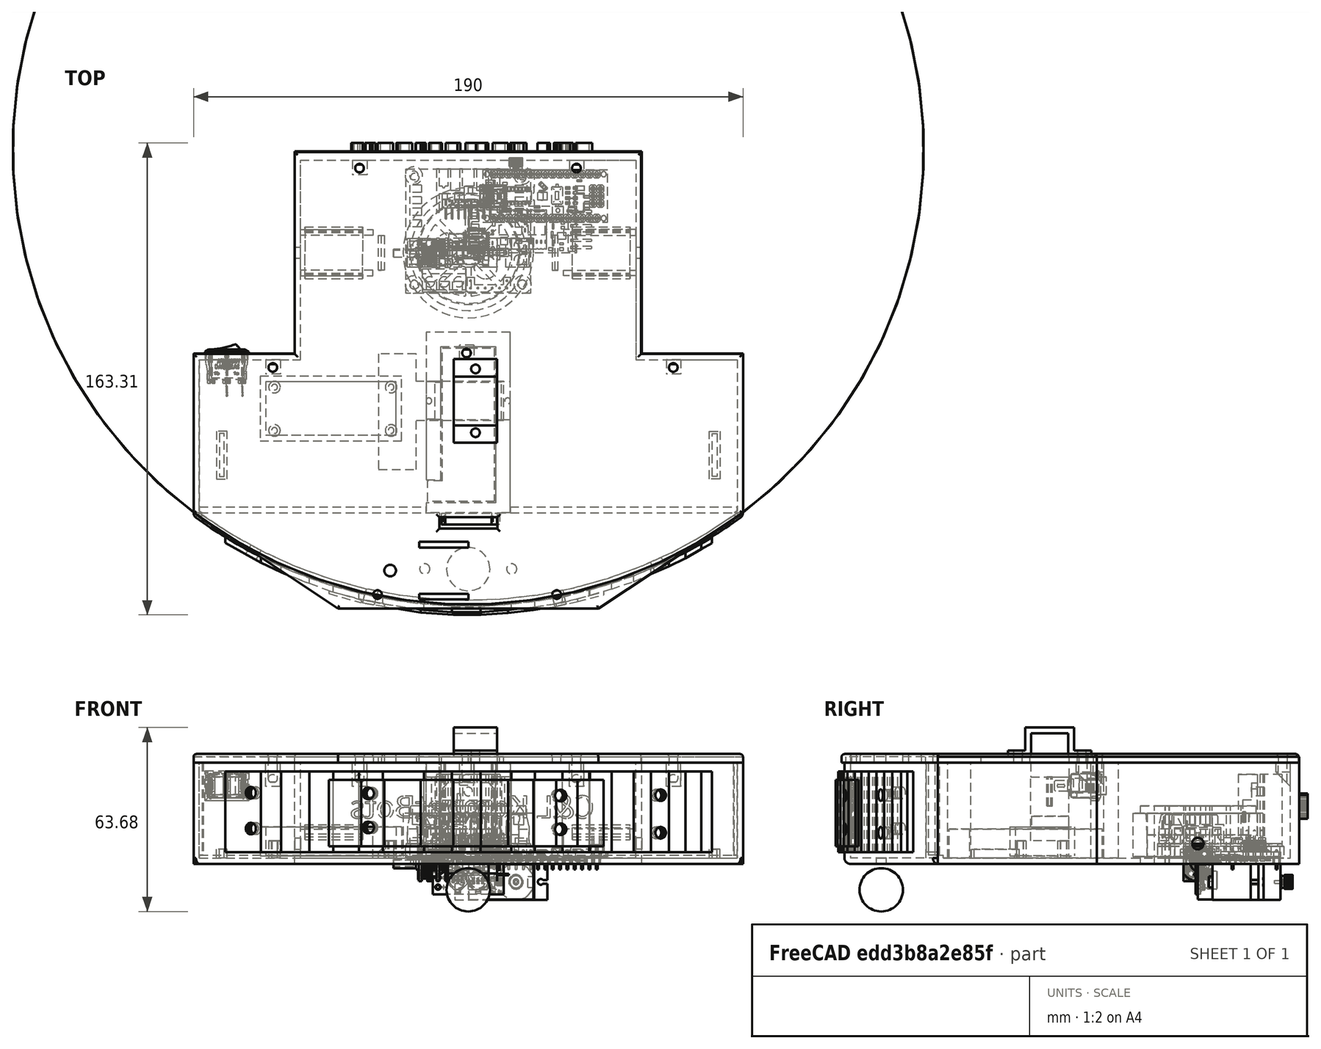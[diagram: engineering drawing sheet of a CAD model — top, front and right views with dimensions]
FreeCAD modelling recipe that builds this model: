
FCSTD DOCUMENT  (FreeCAD 0.20R29410 (Git))
Label: zero_bot
License: All rights reserved
LicenseURL: http://en.wikipedia.org/wiki/All_rights_reserved
objects: Part::Feature×118, Part::Extrusion×50, Sketcher::SketchObject×43, Part::Cut×26, Part::MultiFuse×22, App::Part×10, Part::Box×3, Part::Chamfer×2, Mesh::Feature×2, Part::Part2DObjectPython×1, Part::Fuse×1, Part::Fillet×1, Part::Thickness×1, Part::Sphere×1
note: 269 computed .brp shape members not serialized (recipe doc carries the construction recipe); baked Part::Feature solids carry a one-line shape summary decoded from their .brp

FEATURE [Part::Feature] Part__Feature101  label="Lid Screw Hole001"
  Placement = pos=(159.5,0,0) rot=(0,0,1;0rad)
  shape: bbox 5 x 5 x 8.25 mm, 13 faces (baked)
FEATURE [Part::Feature] Part__Feature102  label="Lid Screw Hole002"
  Placement = pos=(51,69,0) rot=(0,0,1;0rad)
  shape: bbox 5 x 5 x 8.25 mm, 13 faces (baked)
FEATURE [Part::Feature] Part__Feature103  label="Lid Screw Hole003"
  Placement = pos=(126,69,0) rot=(0,0,1;0rad)
  shape: bbox 5 x 5 x 8.25 mm, 13 faces (baked)
FEATURE [Part::Feature] Part__Feature104  label="Lid Screw Hole004"
  Placement = pos=(-120,-158,0) rot=(0,0,1;3.14159rad)
  shape: bbox 5 x 5 x 8.25 mm, 13 faces (baked)
FEATURE [Part::Feature] Part__Feature105  label="Lid Screw Hole005"
  Placement = pos=(-58,-158,0) rot=(0,0,1;3.14159rad)
  shape: bbox 5 x 5 x 8.25 mm, 13 faces (baked)
FEATURE [Part::Feature] Part__Feature106  label="Lid Screw Hole006"
  Placement = pos=(88,5,0) rot=(0,0,1;0rad)
  shape: bbox 5 x 5 x 8.25 mm, 13 faces (baked)
FEATURE [Part::Part2DObjectPython] ShapeString  # Draft 2D object (typed FeaturePython)
  FontFile = <path>
  MakeFace = true
  Placement = pos=(43.52,35,15.82) rot=(0,0.707107,0.707107;3.14159rad)
  Size = 5
  String = C&L KombatBots
  Tracking = 0
FEATURE [Part::Extrusion] Extrude026  label="RobotText"
  Base = -> ShapeString
  Dir = (1e-16,1,4e-16)
  DirMode = 2
  FaceMakerClass = Part::FaceMakerBullseye
  LengthFwd = 3
  LengthRev = 0
  Solid = false
  Symmetric = false
FEATURE [Sketcher::SketchObject] Sketch001
  FullyConstrained = true
  sketch-geometry (10):
    g0: LineSegment StartX=-60 StartY=35 StartZ=0 EndX=60 EndY=35 EndZ=0
    g1: LineSegment StartX=60 StartY=35 StartZ=0 EndX=60 EndY=-35 EndZ=0
    g2: LineSegment StartX=60 StartY=-35 StartZ=0 EndX=95 EndY=-35 EndZ=0
    g3: LineSegment StartX=95 StartY=-35 StartZ=0 EndX=95 EndY=-90 EndZ=0
    g4: LineSegment StartX=95 StartY=-90 StartZ=0 EndX=45 EndY=-123.166 EndZ=0
    g5: LineSegment StartX=45 StartY=-123.166 StartZ=0 EndX=-45 EndY=-123.166 EndZ=0
    g6: LineSegment StartX=-45 StartY=-123.166 StartZ=0 EndX=-95 EndY=-90 EndZ=0
    g7: LineSegment StartX=-95 StartY=-90 StartZ=0 EndX=-95 EndY=-35 EndZ=0
    g8: LineSegment StartX=-95 StartY=-35 StartZ=0 EndX=-60 EndY=-35 EndZ=0
    g9: LineSegment StartX=-60 StartY=-35 StartZ=0 EndX=-60 EndY=35 EndZ=0
  constraints (29):
    c: Horizontal(g0)
    c: Coincident(g0,g1)
    c: Vertical(g1)
    c: Coincident(g1,g2)
    c: Coincident(g2,g3)
    c: Coincident(g3,g4)
    c: Coincident(g4,g5)
    c: Coincident(g5,g6)
    c: Coincident(g6,g7)
    c: Coincident(g7,g8)
    c: Horizontal(g8)
    c: Coincident(g8,g9)
    c: Coincident(g9,g0)
    c: DistanceX(g0,g0) = 120
    c: Vertical(g9)
    c: DistanceY(g9,g9) = 70
    c: DistanceX(g8,g8) = 35
    c: Vertical(g7)
    c: DistanceX(g5,g5) = 90
    c: Horizontal(g5)
    c: Vertical(g3)
    c: DistanceY(g3,g3) = 55
    c: Horizontal(g2)
    c: Equal(g2,g8)
    c: Equal(g9,g1)
    c: Distance(g4) = 60
    c: Equal(g4,g6)
    c: Equal(g3,g7)
    c: Symmetric(g1,g0,g-1)
FEATURE [Part::Extrusion] Extrude001  label="Floor"
  Base = -> Sketch001
  Dir = (0,0,1)
  DirMode = 2
  FaceMakerClass = Part::FaceMakerBullseye
  LengthFwd = 2
  LengthRev = 0
  Solid = true
  Symmetric = false
FEATURE [Sketcher::SketchObject] Sketch002
  FullyConstrained = true
  sketch-geometry (22):
    g0: LineSegment StartX=-60 StartY=35 StartZ=0 EndX=60 EndY=35 EndZ=0
    g1: LineSegment StartX=60 StartY=35 StartZ=0 EndX=60 EndY=-35 EndZ=0
    g2: LineSegment StartX=60 StartY=-35 StartZ=0 EndX=95 EndY=-35 EndZ=0
    g3: LineSegment StartX=95 StartY=-35 StartZ=0 EndX=95 EndY=-90 EndZ=0
    g4: LineSegment StartX=95 StartY=-90 StartZ=0 EndX=45 EndY=-123.166 EndZ=0
    g5: LineSegment StartX=45 StartY=-123.166 StartZ=0 EndX=-45 EndY=-123.166 EndZ=0
    g6: LineSegment StartX=-45 StartY=-123.166 StartZ=0 EndX=-95 EndY=-90 EndZ=0
    g7: LineSegment StartX=-95 StartY=-90 StartZ=0 EndX=-95 EndY=-35 EndZ=0
    g8: LineSegment StartX=-95 StartY=-35 StartZ=0 EndX=-60 EndY=-35 EndZ=0
    g9: LineSegment StartX=-60 StartY=-35 StartZ=0 EndX=-60 EndY=35 EndZ=0
    g10: LineSegment StartX=-58 StartY=32 StartZ=0 EndX=58 EndY=32 EndZ=0
    g11: LineSegment StartX=58 StartY=32 StartZ=0 EndX=58 EndY=-37 EndZ=0
    g12: LineSegment StartX=58 StartY=-37 StartZ=0 EndX=93 EndY=-37 EndZ=0
    g13: LineSegment StartX=93 StartY=-37 StartZ=0 EndX=93 EndY=-89.3266 EndZ=0
    g14: LineSegment StartX=93 StartY=-89.3266 StartZ=0 EndX=45 EndY=-121.166 EndZ=0
    g15: LineSegment StartX=45 StartY=-121.166 StartZ=0 EndX=-45 EndY=-121.166 EndZ=0
    g16: LineSegment StartX=-45 StartY=-121.166 StartZ=0 EndX=-93 EndY=-89.3266 EndZ=0
    g17: LineSegment StartX=-93 StartY=-89.3266 StartZ=0 EndX=-93 EndY=-37 EndZ=0
    g18: LineSegment StartX=-93 StartY=-37 StartZ=0 EndX=-58 EndY=-37 EndZ=0
    g19: LineSegment StartX=-58 StartY=-37 StartZ=0 EndX=-58 EndY=32 EndZ=0
    g20: LineSegment StartX=-45 StartY=-121.166 StartZ=0 EndX=-45 EndY=-123.166 EndZ=0
    g21: LineSegment StartX=45 StartY=-121.166 StartZ=0 EndX=45 EndY=-123.166 EndZ=0
  constraints (63):
    c: Horizontal(g0)
    c: Coincident(g0,g1)
    c: Vertical(g1)
    c: Coincident(g1,g2)
    c: Horizontal(g2)
    c: Coincident(g2,g3)
    c: Vertical(g3)
    c: Coincident(g3,g4)
    c: Coincident(g4,g5)
    c: Horizontal(g5)
    c: Coincident(g5,g6)
    c: Coincident(g6,g7)
    c: Vertical(g7)
    c: Coincident(g7,g8)
    c: Horizontal(g8)
    c: Coincident(g8,g9)
    c: Coincident(g9,g0)
    c: Vertical(g9)
    c: Symmetric(g0,g1,g-1)
    c: DistanceX(g0,g0) = 120
    c: DistanceY(g1,g1) = 70
    c: Equal(g9,g1)
    c: DistanceX(g2,g2) = 35
    c: Equal(g2,g8)
    c: DistanceY(g3,g3) = 55
    c: DistanceX(g5,g5) = 90
    c: Distance(g4) = 60
    c: Equal(g4,g6)
    c: Equal(g3,g7)
    c: Horizontal(g10)
    c: Coincident(g11,g10)
    c: Vertical(g11)
    c: Coincident(g11,g12)
    c: Horizontal(g12)
    c: Coincident(g12,g13)
    c: Vertical(g13)
    c: Coincident(g13,g14)
    c: Coincident(g14,g15)
    c: Horizontal(g15)
    c: Coincident(g15,g16)
    c: Coincident(g16,g17)
    c: Vertical(g17)
    c: Coincident(g17,g18)
    c: Horizontal(g18)
    c: Coincident(g18,g19)
    c: Coincident(g19,g10)
    c: Vertical(g19)
    c: Distance(g10,g0) = 3
    c: Distance(g10,g9) = 2
    c: Distance(g17,g8) = 2
    c: Distance(g16,g7) = 2
    c: Distance(g15,g5) = 2
    c: Distance(g13,g3) = 2
    c: Distance(g12,g2) = 2
    c: Distance(g10,g1) = 2
    c: Coincident(g20,g15)
    c: Coincident(g20,g5)
    c: Coincident(g21,g14)
    c: Coincident(g21,g4)
    c: Vertical(g21)
    c: Vertical(g20)
    c: Parallel(g16,g6)
    c: Parallel(g14,g4)
FEATURE [Part::Extrusion] Extrude002  label="Walls"
  Base = -> Sketch002
  Dir = (0,0,1)
  DirMode = 2
  FaceMakerClass = Part::FaceMakerBullseye
  LengthFwd = 35
  LengthRev = 0
  Solid = true
  Symmetric = false
FEATURE [Part::MultiFuse] Fusion004  label="Body"
  Refine = true
  Shapes = -> [Extrude002,Extrude001]
FEATURE [Sketcher::SketchObject] Sketch003
  FullyConstrained = false
  MapMode = 5
  Placement = pos=(0,0,2) rot=(0,0,1;0rad)
  Support = -> [Fusion004]
  sketch-geometry (36):
    g0: GeomPoint X=25 Y=0 Z=0
    g1: LineSegment StartX=33 StartY=6 StartZ=0 EndX=58 EndY=6 EndZ=0
    g2: LineSegment StartX=58 StartY=6 StartZ=0 EndX=58 EndY=8 EndZ=0
    g3: LineSegment StartX=58 StartY=8 StartZ=0 EndX=33 EndY=8 EndZ=0
    g4: LineSegment StartX=33 StartY=8 StartZ=0 EndX=33 EndY=6 EndZ=0
    g5: GeomPoint X=-25 Y=0 Z=0
    g6: LineSegment StartX=33 StartY=6 StartZ=0 EndX=25 EndY=0 EndZ=0
    g7: GeomPoint X=25 Y=0 Z=0
    g8: LineSegment StartX=32.5993 StartY=-6.5 StartZ=0 EndX=25 EndY=0 EndZ=0
    g9: GeomPoint X=-25 Y=0 Z=0
    g10: GeomPoint X=-25 Y=0 Z=0
    g11: GeomPoint X=25 Y=0 Z=0
    g12: LineSegment StartX=33 StartY=-6 StartZ=0 EndX=58 EndY=-6 EndZ=0
    g13: LineSegment StartX=58 StartY=-6 StartZ=0 EndX=58 EndY=-8 EndZ=0
    g14: LineSegment StartX=58 StartY=-8 StartZ=0 EndX=33 EndY=-8 EndZ=0
    g15: LineSegment StartX=33 StartY=-8 StartZ=0 EndX=33 EndY=-6 EndZ=0
    g16: LineSegment StartX=33 StartY=-6 StartZ=0 EndX=25 EndY=0 EndZ=0
    g17: GeomPoint X=25 Y=0 Z=0
    g18: LineSegment StartX=32.5993 StartY=6.5 StartZ=0 EndX=25 EndY=0 EndZ=0
    g19: GeomPoint X=-25 Y=0 Z=0
    g20: LineSegment StartX=-33 StartY=6 StartZ=0 EndX=-58 EndY=6 EndZ=0
    g21: LineSegment StartX=-58 StartY=6 StartZ=0 EndX=-58 EndY=8 EndZ=0
    g22: LineSegment StartX=-58 StartY=8 StartZ=0 EndX=-33 EndY=8 EndZ=0
    g23: LineSegment StartX=-33 StartY=8 StartZ=0 EndX=-33 EndY=6 EndZ=0
    g24: LineSegment StartX=-33 StartY=6 StartZ=0 EndX=-25 EndY=0 EndZ=0
    g25: GeomPoint X=-25 Y=0 Z=0
    g26: LineSegment StartX=-32.5993 StartY=-6.5 StartZ=0 EndX=-25 EndY=0 EndZ=0
    g27: GeomPoint X=-25 Y=0 Z=0
    g28: LineSegment StartX=-33 StartY=-6 StartZ=0 EndX=-58 EndY=-6 EndZ=0
    g29: LineSegment StartX=-58 StartY=-6 StartZ=0 EndX=-58 EndY=-8 EndZ=0
    g30: LineSegment StartX=-58 StartY=-8 StartZ=0 EndX=-33 EndY=-8 EndZ=0
    g31: LineSegment StartX=-33 StartY=-8 StartZ=0 EndX=-33 EndY=-6 EndZ=0
    g32: LineSegment StartX=-33 StartY=-6 StartZ=0 EndX=-25 EndY=0 EndZ=0
    g33: GeomPoint X=-25 Y=0 Z=0
    g34: LineSegment StartX=-32.5993 StartY=6.5 StartZ=0 EndX=-25 EndY=0 EndZ=0
    g35: LineSegment StartX=-33 StartY=8 StartZ=0 EndX=-33 EndY=-8 EndZ=0
  constraints (60):
    c: PointOnObject(g0,g-1)
    c: Distance(g-1,g0) = 25
    c: Coincident(g1,g2)
    c: Coincident(g2,g3)
    c: Coincident(g3,g4)
    c: Coincident(g4,g1)
    c: Horizontal(g1)
    c: Horizontal(g3)
    c: Vertical(g2)
    c: Vertical(g4)
    c: DistanceY(g4,g4) = 2
    c: DistanceX(g1,g1) = 25
    c: Coincident(g6,g1)
    c: Coincident(g6,g0)
    c: Distance(g6) = 10
    c: DistanceY(g-1,g1) = 6
    c: Coincident(g8,g7)
    c: Distance(g8) = 10
    c: Coincident(g12,g13)
    c: Coincident(g13,g14)
    c: Coincident(g14,g15)
    c: Coincident(g15,g12)
    c: Horizontal(g12)
    c: Horizontal(g14)
    c: Vertical(g13)
    c: Vertical(g15)
    c: Coincident(g16,g12)
    c: Coincident(g16,g11)
    c: Distance(g16) = 10
    c: Coincident(g18,g17)
    c: Distance(g18) = 10
    c: Coincident(g20,g21)
    c: Coincident(g21,g22)
    c: Coincident(g22,g23)
    c: Coincident(g23,g20)
    c: Horizontal(g20)
    c: Horizontal(g22)
    c: Vertical(g21)
    c: Vertical(g23)
    c: Coincident(g24,g20)
    c: Coincident(g24,g19)
    c: Distance(g24) = 10
    c: Coincident(g26,g25)
    c: Distance(g26) = 10
    c: Coincident(g28,g29)
    c: Coincident(g29,g30)
    c: Coincident(g30,g31)
    c: Coincident(g31,g28)
    c: Horizontal(g28)
    c: Horizontal(g30)
    c: Vertical(g29)
    c: Vertical(g31)
    c: Coincident(g32,g28)
    c: Coincident(g32,g27)
    c: Distance(g32) = 10
    c: Coincident(g34,g33)
    c: Distance(g34) = 10
    c: Coincident(g35,g22)
    c: Coincident(g35,g30)
    c: Vertical(g35)
FEATURE [Part::Extrusion] Extrude003  label="motorWalls"
  Base = -> Sketch003
  Dir = (0,0,1)
  DirMode = 2
  FaceMakerClass = Part::FaceMakerBullseye
  LengthFwd = 10
  LengthRev = 0
  Solid = true
  Symmetric = false
FEATURE [Sketcher::SketchObject] Sketch004
  FullyConstrained = false
  MapMode = 5
  Placement = pos=(0,0,2) rot=(0,0,1;0rad)
  Support = -> [Fusion004]
  sketch-geometry (10):
    g0: LineSegment StartX=-31 StartY=6 StartZ=0 EndX=-29 EndY=6 EndZ=0
    g1: LineSegment StartX=-29 StartY=6 StartZ=0 EndX=-29 EndY=-6 EndZ=0
    g2: LineSegment StartX=-29 StartY=-6 StartZ=0 EndX=-31 EndY=-6 EndZ=0
    g3: LineSegment StartX=-31 StartY=-6 StartZ=0 EndX=-31 EndY=6 EndZ=0
    g4: GeomPoint X=-30 Y=0 Z=0
    g5: LineSegment StartX=31 StartY=6 StartZ=0 EndX=29 EndY=6 EndZ=0
    g6: LineSegment StartX=29 StartY=6 StartZ=0 EndX=29 EndY=-6 EndZ=0
    g7: LineSegment StartX=29 StartY=-6 StartZ=0 EndX=31 EndY=-6 EndZ=0
    g8: LineSegment StartX=31 StartY=-6 StartZ=0 EndX=31 EndY=6 EndZ=0
    g9: GeomPoint X=30 Y=0 Z=0
  constraints (22):
    c: Coincident(g0,g1)
    c: Coincident(g1,g2)
    c: Coincident(g2,g3)
    c: Coincident(g3,g0)
    c: Horizontal(g0)
    c: Horizontal(g2)
    c: Vertical(g1)
    c: Vertical(g3)
    c: PointOnObject(g4,g-1)
    c: Distance(g-1,g4) = 30
    c: Symmetric(g0,g2,g4)
    c: DistanceX(g0,g0) = 2
    c: DistanceY(g1,g1) = 12
    c: Coincident(g5,g6)
    c: Coincident(g6,g7)
    c: Coincident(g7,g8)
    c: Coincident(g8,g5)
    c: Horizontal(g5)
    c: Horizontal(g7)
    c: Vertical(g6)
    c: Vertical(g8)
    c: Symmetric(g5,g7,g9)
FEATURE [Part::Extrusion] Extrude004
  Base = -> Sketch004
  Dir = (0,0,1)
  DirMode = 2
  FaceMakerClass = Part::FaceMakerBullseye
  LengthFwd = 3
  LengthRev = 0
  Solid = true
  Symmetric = false
FEATURE [Part::Chamfer] Chamfer  label="MotorSlotter"
  Base = -> Extrude004
  Edges = 2 edges r=1: [Edge12,Edge24]
FEATURE [Part::MultiFuse] Fusion001  label="MotorHolders"
  Refine = true
  Shapes = -> [Chamfer,Extrude003]
FEATURE [Part::MultiFuse] Fusion005
  Refine = true
  Shapes = -> [Fusion001,Fusion004]
FEATURE [Sketcher::SketchObject] Sketch005
  FullyConstrained = true
  MapMode = 5
  Placement = pos=(0,0,2) rot=(0,0,1;0rad)
  Support = -> [Fusion005]
  sketch-geometry (8):
    g0: Circle CenterX=-18.8 CenterY=26.75 CenterZ=0 NormalX=0 NormalY=0 NormalZ=1 AngleXU=0 Radius=3
    g1: Circle CenterX=-18.8 CenterY=26.75 CenterZ=0 NormalX=0 NormalY=0 NormalZ=1 AngleXU=0 Radius=1.5
    g2: Circle CenterX=18.8 CenterY=26.75 CenterZ=0 NormalX=0 NormalY=0 NormalZ=1 AngleXU=0 Radius=3
    g3: Circle CenterX=18.8 CenterY=26.75 CenterZ=0 NormalX=0 NormalY=0 NormalZ=1 AngleXU=0 Radius=1.5
    g4: Circle CenterX=18.8 CenterY=-11 CenterZ=0 NormalX=0 NormalY=0 NormalZ=1 AngleXU=0 Radius=3
    g5: Circle CenterX=18.8 CenterY=-11 CenterZ=0 NormalX=0 NormalY=0 NormalZ=1 AngleXU=0 Radius=1.5
    g6: Circle CenterX=-18.8 CenterY=-11 CenterZ=0 NormalX=0 NormalY=0 NormalZ=1 AngleXU=0 Radius=3
    g7: Circle CenterX=-18.8 CenterY=-11 CenterZ=0 NormalX=0 NormalY=0 NormalZ=1 AngleXU=0 Radius=1.5
  constraints (20):
    c: Coincident(g1,g0)
    c: Coincident(g3,g2)
    c: Coincident(g5,g4)
    c: Coincident(g7,g6)
    c: DistanceX(g-2,g6) = -18.8
    c: Diameter(g7) = 3
    c: Diameter(g6) = 6
    c: DistanceY(g-1,g6) = -11
    c: DistanceY(g-1,g4) = -11
    c: DistanceX(g-2,g4) = 18.8
    c: Diameter(g5) = 3
    c: Diameter(g4) = 6
    c: DistanceY(g-1,g2) = 26.75
    c: DistanceY(g-1,g0) = 26.75
    c: DistanceX(g-2,g2) = 18.8
    c: DistanceX(g-2,g0) = -18.8
    c: Diameter(g1) = 3
    c: Diameter(g0) = 6
    c: Diameter(g2) = 6
    c: Diameter(g3) = 3
FEATURE [Part::Extrusion] Extrude005  label="L289N Holder"
  Base = -> Sketch005
  Dir = (0,0,1)
  DirMode = 2
  FaceMakerClass = Part::FaceMakerBullseye
  LengthFwd = 4
  LengthRev = 0
  Solid = true
  Symmetric = false
FEATURE [Part::MultiFuse] Fusion006
  Refine = true
  Shapes = -> [Extrude005,Fusion005]
FEATURE [Sketcher::SketchObject] Sketch006
  FullyConstrained = true
  MapMode = 5
  Placement = pos=(60,0,0) rot=(0.57735,0.57735,0.57735;2.0944rad)
  Support = -> [Fusion006]
  sketch-geometry (1):
    g0: Circle CenterX=0 CenterY=7 CenterZ=0 NormalX=0 NormalY=0 NormalZ=1 AngleXU=0 Radius=2
  constraints (3):
    c: PointOnObject(g0,g-2)
    c: Diameter(g0) = 4
    c: Distance(g0,g-1) = 7
FEATURE [Part::Extrusion] Extrude006
  Base = -> Sketch006
  Dir = (1,0,0)
  DirMode = 2
  FaceMakerClass = Part::FaceMakerBullseye
  LengthFwd = 10
  LengthRev = 0
  Solid = true
  Symmetric = true
FEATURE [Sketcher::SketchObject] Sketch007
  FullyConstrained = true
  MapMode = 5
  Placement = pos=(-60,0,0) rot=(0.57735,-0.57735,-0.57735;2.0944rad)
  Support = -> [Fusion006]
  sketch-geometry (1):
    g0: Circle CenterX=0 CenterY=7 CenterZ=0 NormalX=0 NormalY=0 NormalZ=1 AngleXU=0 Radius=2
  constraints (3):
    c: PointOnObject(g0,g-2)
    c: Diameter(g0) = 4
    c: Distance(g-1,g0) = 7
FEATURE [Part::Extrusion] Extrude007
  Base = -> Sketch007
  Dir = (-1,0,0)
  DirMode = 2
  FaceMakerClass = Part::FaceMakerBullseye
  LengthFwd = 10
  LengthRev = 0
  Solid = true
  Symmetric = true
FEATURE [Part::MultiFuse] Fusion007  label="Motor Gaps"
  Refine = true
  Shapes = -> [Extrude006,Extrude007]
FEATURE [Part::Cut] Cut005
  Base = -> Fusion006
  Refine = true
  Tool = -> Fusion007
FEATURE [Sketcher::SketchObject] Sketch008
  FullyConstrained = false
  MapMode = 5
  Placement = pos=(0,-35,0) rot=(0,0.707107,0.707107;3.14159rad)
  Support = -> [Cut005]
  sketch-geometry (4):
    g0: LineSegment StartX=90.8327 StartY=31.6367 StartZ=0 EndX=76.0827 EndY=31.6367 EndZ=0
    g1: LineSegment StartX=76.0827 StartY=31.6367 StartZ=0 EndX=76.0827 EndY=21.8867 EndZ=0
    g2: LineSegment StartX=76.0827 StartY=21.8867 StartZ=0 EndX=90.8327 EndY=21.8867 EndZ=0
    g3: LineSegment StartX=90.8327 StartY=21.8867 StartZ=0 EndX=90.8327 EndY=31.6367 EndZ=0
  constraints (8):
    c: Coincident(g0,g1)
    c: Coincident(g1,g2)
    c: Coincident(g2,g3)
    c: Coincident(g3,g0)
    c: Horizontal(g0)
    c: Horizontal(g2)
    c: Vertical(g1)
    c: Vertical(g3)
FEATURE [Part::Extrusion] Extrude008  label="InterruptGap"
  Base = -> Sketch008
  Dir = (0,1,-2e-16)
  DirMode = 2
  FaceMakerClass = Part::FaceMakerBullseye
  LengthFwd = 10
  LengthRev = 0
  Solid = true
  Symmetric = true
FEATURE [Part::Cut] Cut006
  Base = -> Cut005
  Refine = true
  Tool = -> Extrude008
FEATURE [Sketcher::SketchObject] Sketch009
  FullyConstrained = false
  MapMode = 5
  Placement = pos=(0,0,2) rot=(0,0,1;0rad)
  Support = -> [Cut006]
  sketch-geometry (20):
    g0: LineSegment StartX=83.4 StartY=-61.75 StartZ=0 EndX=87 EndY=-61.75 EndZ=0
    g1: LineSegment StartX=87 StartY=-61.75 StartZ=0 EndX=87 EndY=-78.25 EndZ=0
    g2: LineSegment StartX=87 StartY=-78.25 StartZ=0 EndX=83.4 EndY=-78.25 EndZ=0
    g3: LineSegment StartX=83.4 StartY=-78.25 StartZ=0 EndX=83.4 EndY=-61.75 EndZ=0
    g4: LineSegment StartX=84.4 StartY=-62.6 StartZ=0 EndX=86 EndY=-62.6 EndZ=0
    g5: LineSegment StartX=86 StartY=-62.6 StartZ=0 EndX=86 EndY=-77.4 EndZ=0
    g6: LineSegment StartX=86 StartY=-77.4 StartZ=0 EndX=84.4 EndY=-77.4 EndZ=0
    g7: LineSegment StartX=84.4 StartY=-77.4 StartZ=0 EndX=84.4 EndY=-62.6 EndZ=0
    g8: GeomPoint X=93 Y=-70 Z=0
    g9: LineSegment StartX=-0.686599 StartY=-70 StartZ=0 EndX=93 EndY=-70 EndZ=0
    g10: LineSegment StartX=-83.4 StartY=-61.75 StartZ=0 EndX=-87 EndY=-61.75 EndZ=0
    g11: LineSegment StartX=-87 StartY=-61.75 StartZ=0 EndX=-87 EndY=-78.25 EndZ=0
    g12: LineSegment StartX=-87 StartY=-78.25 StartZ=0 EndX=-83.4 EndY=-78.25 EndZ=0
    g13: LineSegment StartX=-83.4 StartY=-78.25 StartZ=0 EndX=-83.4 EndY=-61.75 EndZ=0
    g14: LineSegment StartX=-84.4 StartY=-62.6 StartZ=0 EndX=-86 EndY=-62.6 EndZ=0
    g15: LineSegment StartX=-86 StartY=-62.6 StartZ=0 EndX=-86 EndY=-77.4 EndZ=0
    g16: LineSegment StartX=-86 StartY=-77.4 StartZ=0 EndX=-84.4 EndY=-77.4 EndZ=0
    g17: LineSegment StartX=-84.4 StartY=-77.4 StartZ=0 EndX=-84.4 EndY=-62.6 EndZ=0
    g18: GeomPoint X=-93 Y=-70 Z=0
    g19: LineSegment StartX=0.686599 StartY=-70 StartZ=0 EndX=-93 EndY=-70 EndZ=0
  constraints (46):
    c: Coincident(g0,g1)
    c: Coincident(g1,g2)
    c: Coincident(g2,g3)
    c: Coincident(g3,g0)
    c: Horizontal(g0)
    c: Horizontal(g2)
    c: Vertical(g1)
    c: Vertical(g3)
    c: Coincident(g4,g5)
    c: Coincident(g5,g6)
    c: Coincident(g6,g7)
    c: Coincident(g7,g4)
    c: Horizontal(g4)
    c: Horizontal(g6)
    c: Vertical(g7)
    c: DistanceX(g-2,g8) = 93
    c: DistanceY(g-1,g8) = -70
    c: Distance(g8,g1) = 6
    c: Coincident(g9,g8)
    c: Symmetric(g1,g0,g9)
    c: DistanceY(g1,g1) = 16.5
    c: Symmetric(g4,g5,g9)
    c: DistanceY(g5,g5) = 14.8
    c: DistanceX(g0,g0) = 3.6
    c: DistanceX(g4,g4) = 1.6
    c: Distance(g4,g1) = 1
    c: Coincident(g10,g11)
    c: Coincident(g11,g12)
    c: Coincident(g12,g13)
    c: Coincident(g13,g10)
    c: Horizontal(g10)
    c: Horizontal(g12)
    c: Vertical(g11)
    c: Vertical(g13)
    c: Coincident(g14,g15)
    c: Coincident(g15,g16)
    c: Coincident(g16,g17)
    c: Coincident(g17,g14)
    c: Horizontal(g14)
    c: Horizontal(g16)
    c: Vertical(g17)
    c: Distance(g18,g11) = 6
    c: Coincident(g19,g18)
    c: Symmetric(g11,g10,g19)
    c: Symmetric(g14,g15,g19)
    c: Distance(g14,g11) = 1
FEATURE [Part::Extrusion] Extrude009  label="HitSensorHolders"
  Base = -> Sketch009
  Dir = (0,0,1)
  DirMode = 2
  FaceMakerClass = Part::FaceMakerBullseye
  LengthFwd = 3
  LengthRev = 0
  Solid = true
  Symmetric = false
FEATURE [Part::MultiFuse] Fusion008
  Refine = true
  Shapes = -> [Cut006,Extrude009]
FEATURE [Sketcher::SketchObject] Sketch010
  FullyConstrained = true
  sketch-geometry (11):
    g0: LineSegment StartX=-14.5 StartY=-78.5 StartZ=0 EndX=-9.5 EndY=-78.5 EndZ=0
    g1: LineSegment StartX=-9.5 StartY=-78.5 StartZ=0 EndX=-9.5 EndY=-32.5 EndZ=0
    g2: LineSegment StartX=-9.5 StartY=-32.5 StartZ=0 EndX=9.5 EndY=-32.5 EndZ=0
    g3: LineSegment StartX=9.5 StartY=-32.5 StartZ=0 EndX=9.5 EndY=-86.5 EndZ=0
    g4: LineSegment StartX=9.5 StartY=-86.5 StartZ=0 EndX=-14.5 EndY=-86.5 EndZ=0
    g5: LineSegment StartX=-14.5 StartY=-86.5 StartZ=0 EndX=-14.5 EndY=-91.5 EndZ=0
    g6: LineSegment StartX=-14.5 StartY=-91.5 StartZ=0 EndX=14.5 EndY=-91.5 EndZ=0
    g7: LineSegment StartX=14.5 StartY=-91.5 StartZ=0 EndX=14.5 EndY=-27.5 EndZ=0
    g8: LineSegment StartX=14.5 StartY=-27.5 StartZ=0 EndX=-14.5 EndY=-27.5 EndZ=0
    g9: LineSegment StartX=-14.5 StartY=-27.5 StartZ=0 EndX=-14.5 EndY=-78.5 EndZ=0
    g10: GeomPoint X=0 Y=-59.5 Z=0
  constraints (30):
    c: Horizontal(g0)
    c: Coincident(g0,g1)
    c: Vertical(g1)
    c: Coincident(g1,g2)
    c: Horizontal(g2)
    c: Coincident(g2,g3)
    c: Vertical(g3)
    c: Coincident(g3,g4)
    c: Horizontal(g4)
    c: Coincident(g4,g5)
    c: Vertical(g5)
    c: Coincident(g5,g6)
    c: Horizontal(g6)
    c: Coincident(g6,g7)
    c: Vertical(g7)
    c: Coincident(g7,g8)
    c: Horizontal(g8)
    c: Coincident(g8,g9)
    c: Coincident(g9,g0)
    c: Vertical(g9)
    c: DistanceX(g2,g2) = 19
    c: PointOnObject(g10,g-2)
    c: DistanceY(g10,g-1) = 59.5
    c: Symmetric(g3,g1,g10)
    c: Symmetric(g6,g8,g10)
    c: DistanceX(g8,g8) = 29
    c: DistanceY(g3,g3) = 54
    c: DistanceY(g7,g7) = 64
    c: DistanceY(g1,g1) = 46
    c: DistanceX(g6,g6) = 29
FEATURE [Part::Extrusion] Extrude010  label="Battery Gap"
  Base = -> Sketch010
  Dir = (0,0,1)
  DirMode = 2
  FaceMakerClass = Part::FaceMakerBullseye
  LengthFwd = 35
  LengthRev = 0
  Solid = true
  Symmetric = false
FEATURE [Part::MultiFuse] Fusion009
  Refine = true
  Shapes = -> [Extrude010,Fusion008]
FEATURE [Sketcher::SketchObject] Sketch011
  FullyConstrained = false
  MapMode = 5
  Placement = pos=(0,0,2) rot=(0,0,1;0rad)
  Support = -> [Fusion009]
  sketch-geometry (13):
    g0: LineSegment StartX=-52.8 StartY=-54 StartZ=0 EndX=0 EndY=-54 EndZ=0
    g1: LineSegment StartX=-52.8 StartY=-54 StartZ=0 EndX=-84.748 EndY=-54 EndZ=0
    g2: Circle CenterX=-66.9946 CenterY=-46.5 CenterZ=0 NormalX=0 NormalY=0 NormalZ=1 AngleXU=0 Radius=1
    g3: Circle CenterX=-66.9946 CenterY=-46.5 CenterZ=0 NormalX=0 NormalY=0 NormalZ=1 AngleXU=0 Radius=2
    g4: Circle CenterX=-66.9946 CenterY=-61.5 CenterZ=0 NormalX=0 NormalY=0 NormalZ=1 AngleXU=0 Radius=1
    g5: Circle CenterX=-66.9946 CenterY=-61.5 CenterZ=0 NormalX=0 NormalY=0 NormalZ=1 AngleXU=0 Radius=2
    g6: GeomPoint X=-25.3 Y=-54 Z=0
    g7: Circle CenterX=-26.6711 CenterY=-46.5 CenterZ=0 NormalX=0 NormalY=0 NormalZ=1 AngleXU=0 Radius=1
    g8: Circle CenterX=-26.6711 CenterY=-46.5 CenterZ=0 NormalX=0 NormalY=0 NormalZ=1 AngleXU=0 Radius=2
    g9: Circle CenterX=-26.6711 CenterY=-61.5 CenterZ=0 NormalX=0 NormalY=0 NormalZ=1 AngleXU=0 Radius=1
    g10: Circle CenterX=-26.6711 CenterY=-61.5 CenterZ=0 NormalX=0 NormalY=0 NormalZ=1 AngleXU=0 Radius=2
    g11: LineSegment StartX=-52.8 StartY=-54 StartZ=0 EndX=0 EndY=-54 EndZ=0
    g12: GeomPoint X=-25.3 Y=-54 Z=0
  constraints (24):
    c: DistanceY(g0,g-1) = 54
    c: PointOnObject(g0,g-2)
    c: Horizontal(g0)
    c: Coincident(g1,g0)
    c: Horizontal(g1)
    c: Coincident(g3,g2)
    c: Diameter(g2) = 2
    c: Diameter(g3) = 4
    c: Distance(g2,g1) = 7.5
    c: Coincident(g5,g4)
    c: Diameter(g4) = 2
    c: Diameter(g5) = 4
    c: PointOnObject(g6,g0)
    c: DistanceX(g6,g-1) = 25.3
    c: Coincident(g8,g7)
    c: Diameter(g7) = 2
    c: Diameter(g8) = 4
    c: Distance(g7,g0) = 7.5
    c: Horizontal(g11)
    c: PointOnObject(g12,g11)
    c: Coincident(g10,g9)
    c: Diameter(g9) = 2
    c: Diameter(g10) = 4
    c: Distance(g9,g11) = 7.5
FEATURE [Part::Extrusion] Extrude011  label="Arduino Holder"
  Base = -> Sketch011
  Dir = (0,0,1)
  DirMode = 2
  FaceMakerClass = Part::FaceMakerBullseye
  LengthFwd = 6
  LengthRev = 0
  Solid = true
  Symmetric = false
FEATURE [Part::MultiFuse] Fusion010
  Refine = true
  Shapes = -> [Fusion009,Extrude011]
FEATURE [Sketcher::SketchObject] Sketch012
  FullyConstrained = true
  MapMode = 5
  Placement = pos=(0,-91.5,0) rot=(1,0,0;1.5708rad)
  Support = -> [Extrude010]
  sketch-geometry (10):
    g0: LineSegment StartX=8 StartY=35 StartZ=0 EndX=10 EndY=35 EndZ=0
    g1: LineSegment StartX=10 StartY=35 StartZ=0 EndX=10 EndY=2 EndZ=0
    g2: LineSegment StartX=10 StartY=2 StartZ=0 EndX=-10 EndY=2 EndZ=0
    g3: LineSegment StartX=-10 StartY=2 StartZ=0 EndX=-10 EndY=35 EndZ=0
    g4: LineSegment StartX=-10 StartY=35 StartZ=0 EndX=-8 EndY=35 EndZ=0
    g5: LineSegment StartX=-8 StartY=35 StartZ=0 EndX=-8 EndY=4 EndZ=0
    g6: LineSegment StartX=-8 StartY=4 StartZ=0 EndX=8 EndY=4 EndZ=0
    g7: LineSegment StartX=8 StartY=4 StartZ=0 EndX=8 EndY=35 EndZ=0
    g8: GeomPoint X=0 Y=2 Z=0
    g9: LineSegment StartX=0 StartY=2 StartZ=0 EndX=0 EndY=0 EndZ=0
  constraints (28):
    c: Horizontal(g0)
    c: Coincident(g0,g1)
    c: Vertical(g1)
    c: Coincident(g1,g2)
    c: Coincident(g2,g3)
    c: Vertical(g3)
    c: Coincident(g3,g4)
    c: Horizontal(g4)
    c: Coincident(g4,g5)
    c: Vertical(g5)
    c: Coincident(g5,g6)
    c: Horizontal(g6)
    c: Coincident(g6,g7)
    c: Coincident(g7,g0)
    c: Vertical(g7)
    c: DistanceX(g0,g0) = 2
    c: Equal(g4,g0)
    c: DistanceX(g6,g6) = 16
    c: DistanceY(g1,g1) = 33
    c: Equal(g3,g1)
    c: Distance(g6,g2) = 2
    c: Horizontal(g2)
    c: PointOnObject(g8,g2)
    c: DistanceX(g8,g1) = 10
    c: DistanceY(g-1,g1) = 2
    c: Coincident(g9,g8)
    c: Coincident(g9,g-1)
    c: Vertical(g9)
FEATURE [Part::Extrusion] Extrude012  label="Bluetooth Module Holder"
  Base = -> Sketch012
  Dir = (0,-1,2e-16)
  DirMode = 2
  FaceMakerClass = Part::FaceMakerBullseye
  LengthFwd = 4
  LengthRev = 0
  Solid = true
  Symmetric = false
FEATURE [Part::MultiFuse] Fusion011
  Refine = true
  Shapes = -> [Fusion010,Extrude012]
FEATURE [Sketcher::SketchObject] Sketch013
  FullyConstrained = false
  MapMode = 5
  Placement = pos=(4.907e-13,3.136e-13,35) rot=(0,0,1;0rad)
  Support = -> [Fusion011]
  sketch-geometry (8):
    g0: LineSegment StartX=8 StartY=-92.5 StartZ=0 EndX=8.5 EndY=-92.5 EndZ=0
    g1: LineSegment StartX=8.5 StartY=-92.5 StartZ=0 EndX=8.5 EndY=-94.7 EndZ=0
    g2: LineSegment StartX=8.5 StartY=-94.7 StartZ=0 EndX=8 EndY=-94.7 EndZ=0
    g3: LineSegment StartX=8 StartY=-94.7 StartZ=0 EndX=8 EndY=-92.5 EndZ=0
    g4: LineSegment StartX=-8 StartY=-92.5 StartZ=0 EndX=-8.5 EndY=-92.5 EndZ=0
    g5: LineSegment StartX=-8.5 StartY=-92.5 StartZ=0 EndX=-8.5 EndY=-94.7 EndZ=0
    g6: LineSegment StartX=-8.5 StartY=-94.7 StartZ=0 EndX=-8 EndY=-94.7 EndZ=0
    g7: LineSegment StartX=-8 StartY=-94.7 StartZ=0 EndX=-8 EndY=-92.5 EndZ=0
  constraints (20):
    c: Coincident(g0,g1)
    c: Coincident(g1,g2)
    c: Coincident(g2,g3)
    c: Coincident(g3,g0)
    c: Horizontal(g0)
    c: Horizontal(g2)
    c: Vertical(g1)
    c: Vertical(g3)
    c: DistanceY(g1,g1) = 2.2
    c: DistanceX(g0,g0) = 0.5
    c: DistanceX(g-2,g0) = 8
    c: DistanceY(g-1,g0) = -92.5
    c: Coincident(g4,g5)
    c: Coincident(g5,g6)
    c: Coincident(g6,g7)
    c: Coincident(g7,g4)
    c: Horizontal(g4)
    c: Horizontal(g6)
    c: Vertical(g5)
    c: Vertical(g7)
FEATURE [Part::Extrusion] Extrude013  label="Bluetooth Module Slotter"
  Base = -> Sketch013
  Dir = (1.4e-14,9e-15,1)
  DirMode = 2
  FaceMakerClass = Part::FaceMakerBullseye
  LengthFwd = -32
  LengthRev = 0
  Solid = true
  Symmetric = false
FEATURE [Part::Cut] Cut007
  Base = -> Fusion011
  Refine = true
  Tool = -> Extrude013
FEATURE [Sketcher::SketchObject] Sketch014
  FullyConstrained = false
  MapMode = 5
  Placement = pos=(0,-37,0) rot=(1,0,0;1.5708rad)
  Support = -> [Cut007]
  sketch-geometry (4):
    g0: LineSegment StartX=-91.0267 StartY=31.7549 StartZ=0 EndX=-86.0267 EndY=31.7549 EndZ=0
    g1: LineSegment StartX=-86.0267 StartY=31.7549 StartZ=0 EndX=-86.0267 EndY=26.7549 EndZ=0
    g2: LineSegment StartX=-86.0267 StartY=26.7549 StartZ=0 EndX=-91.0267 EndY=26.7549 EndZ=0
    g3: LineSegment StartX=-91.0267 StartY=26.7549 StartZ=0 EndX=-91.0267 EndY=31.7549 EndZ=0
  constraints (10):
    c: Coincident(g0,g1)
    c: Coincident(g1,g2)
    c: Coincident(g2,g3)
    c: Coincident(g3,g0)
    c: Horizontal(g0)
    c: Horizontal(g2)
    c: Vertical(g1)
    c: Vertical(g3)
    c: DistanceX(g0,g0) = 5
    c: DistanceY(g1,g1) = 5
FEATURE [Part::Extrusion] Extrude014
  Base = -> Sketch014
  Dir = (0,-1,2e-16)
  DirMode = 2
  FaceMakerClass = Part::FaceMakerBullseye
  LengthFwd = 5
  LengthRev = 0
  Solid = true
  Symmetric = false
FEATURE [Part::Chamfer] Chamfer001  label="Bot Screw Holder"
  Base = -> Extrude014
  Edges = 1 edges r=4.99: [Edge10]
FEATURE [Sketcher::SketchObject] Sketch015
  FullyConstrained = true
  MapMode = 5
  Placement = pos=(0,7e-15,31.7549) rot=(0,0,1;0rad)
  Support = -> [Chamfer001]
  sketch-geometry (1):
    g0: Circle CenterX=-88.6 CenterY=-39.7 CenterZ=0 NormalX=0 NormalY=0 NormalZ=1 AngleXU=0 Radius=1.5
  constraints (3):
    c: Diameter(g0) = 3
    c: DistanceX(g-2,g0) = -88.6
    c: DistanceY(g-1,g0) = -39.7
FEATURE [Part::Extrusion] Extrude015  label="Screw Hole"
  Base = -> Sketch015
  Dir = (0,2e-16,1)
  DirMode = 2
  FaceMakerClass = Part::FaceMakerBullseye
  LengthFwd = -8
  LengthRev = 0
  Placement = pos=(0,0,4.5) rot=(0,0,1;0rad)
  Solid = true
  Symmetric = false
FEATURE [Sketcher::SketchObject] Sketch016
  FullyConstrained = false
  MapMode = 5
  Placement = pos=(0,7e-15,31.7549) rot=(0,0,1;0rad)
  Support = -> [Chamfer001]
  sketch-geometry (4):
    g0: LineSegment StartX=-91.0267 StartY=-37 StartZ=0 EndX=-86.0267 EndY=-37 EndZ=0
    g1: LineSegment StartX=-86.0267 StartY=-37 StartZ=0 EndX=-86.0267 EndY=-42 EndZ=0
    g2: LineSegment StartX=-86.0267 StartY=-42 StartZ=0 EndX=-91.0267 EndY=-42 EndZ=0
    g3: LineSegment StartX=-91.0267 StartY=-42 StartZ=0 EndX=-91.0267 EndY=-37 EndZ=0
  constraints (10):
    c: Coincident(g0,g1)
    c: Coincident(g1,g2)
    c: Coincident(g2,g3)
    c: Coincident(g3,g0)
    c: Horizontal(g0)
    c: Horizontal(g2)
    c: Vertical(g1)
    c: Vertical(g3)
    c: DistanceY(g1,g1) = 5
    c: DistanceX(g2,g2) = 5
FEATURE [Part::Extrusion] Extrude016  label="Top Screw Holder"
  Base = -> Sketch016
  Dir = (0,2e-16,1)
  DirMode = 2
  FaceMakerClass = Part::FaceMakerBullseye
  LengthFwd = 3.25
  LengthRev = 0
  Solid = true
  Symmetric = false
FEATURE [Part::Fuse] Fusion012
  Base = -> Chamfer001
  Refine = true
  Tool = -> Extrude016
FEATURE [Part::Cut] Cut008  label="Lid Screw Hole"
  Base = -> Fusion012
  Placement = pos=(21,0,0) rot=(0,0,1;0rad)
  Refine = true
  Tool = -> Extrude015
FEATURE [Part::MultiFuse] Fusion013  label="Lid Screw Holes"
  Refine = true
  Shapes = -> [Cut008,Part__Feature101,Part__Feature102,Part__Feature103,Part__Feature104,Part__Feature105,Part__Feature106]
FEATURE [Part::MultiFuse] Fusion014
  Refine = true
  Shapes = -> [Cut007,Fusion013]
FEATURE [Sketcher::SketchObject] Sketch017
  FullyConstrained = false
  MapMode = 5
  Placement = pos=(70.4856,-106.261,0) rot=(0.919866,0.27735,0.27735;1.65423rad)
  Support = -> [Fusion014]
  sketch-geometry (4):
    g0: Circle CenterX=15 CenterY=27 CenterZ=0 NormalX=0 NormalY=0 NormalZ=1 AngleXU=0 Radius=2
    g1: Circle CenterX=15 CenterY=8 CenterZ=0 NormalX=0 NormalY=0 NormalZ=1 AngleXU=0 Radius=2
    g2: Circle CenterX=-15 CenterY=27 CenterZ=0 NormalX=0 NormalY=0 NormalZ=1 AngleXU=0 Radius=2
    g3: Circle CenterX=-15 CenterY=8 CenterZ=0 NormalX=0 NormalY=0 NormalZ=1 AngleXU=0 Radius=2
  constraints (9):
    c: Diameter(g1) = 4
    c: Diameter(g0) = 4
    c: DistanceX(g-2,g0) = 15
    c: DistanceX(g-2,g1) = 15
    c: Distance(g1,g0) = 19
    c: DistanceY(g-1,g1) = 8
    c: Diameter(g3) = 4
    c: Diameter(g2) = 4
    c: Distance(g3,g2) = 19
FEATURE [Part::Extrusion] Extrude017
  Base = -> Sketch017
  Dir = (0.552771,-0.833333,-5e-16)
  DirMode = 2
  FaceMakerClass = Part::FaceMakerBullseye
  LengthFwd = 10
  LengthRev = 0
  Solid = true
  Symmetric = true
FEATURE [Sketcher::SketchObject] Sketch018
  FullyConstrained = false
  MapMode = 5
  Placement = pos=(-70.4856,-106.261,0) rot=(0.919866,-0.27735,-0.27735;1.65423rad)
  Support = -> [Fusion014]
  sketch-geometry (4):
    g0: Circle CenterX=-15 CenterY=8 CenterZ=0 NormalX=0 NormalY=0 NormalZ=1 AngleXU=0 Radius=2
    g1: Circle CenterX=-15 CenterY=27 CenterZ=0 NormalX=0 NormalY=0 NormalZ=1 AngleXU=0 Radius=2
    g2: Circle CenterX=15 CenterY=8 CenterZ=0 NormalX=0 NormalY=0 NormalZ=1 AngleXU=0 Radius=2
    g3: Circle CenterX=15 CenterY=27 CenterZ=0 NormalX=0 NormalY=0 NormalZ=1 AngleXU=0 Radius=2
  constraints (9):
    c: Diameter(g1) = 4
    c: Distance(g1,g0) = 19
    c: DistanceY(g-1,g0) = 8
    c: DistanceX(g-2,g0) = -15
    c: DistanceX(g-2,g1) = -15
    c: Diameter(g0) = 4
    c: Diameter(g3) = 4
    c: Distance(g3,g2) = 19
    c: Diameter(g2) = 4
FEATURE [Part::Extrusion] Extrude018
  Base = -> Sketch018
  Dir = (-0.552771,-0.833333,0)
  DirMode = 2
  FaceMakerClass = Part::FaceMakerBullseye
  LengthFwd = 10
  LengthRev = 0
  Solid = true
  Symmetric = true
FEATURE [Sketcher::SketchObject] Sketch019
  FullyConstrained = false
  MapMode = 5
  Placement = pos=(0,-123.166,0) rot=(1,0,0;1.5708rad)
  Support = -> [Fusion014]
  sketch-geometry (4):
    g0: Circle CenterX=-25 CenterY=27 CenterZ=0 NormalX=0 NormalY=0 NormalZ=1 AngleXU=0 Radius=2
    g1: Circle CenterX=-25 CenterY=8 CenterZ=0 NormalX=0 NormalY=0 NormalZ=1 AngleXU=0 Radius=2
    g2: Circle CenterX=25 CenterY=27 CenterZ=0 NormalX=0 NormalY=0 NormalZ=1 AngleXU=0 Radius=2
    g3: Circle CenterX=25 CenterY=8 CenterZ=0 NormalX=0 NormalY=0 NormalZ=1 AngleXU=0 Radius=2
  constraints (9):
    c: Equal(g0,g1)
    c: Diameter(g0) = 4
    c: DistanceY(g-1,g1) = 8
    c: Distance(g1,g0) = 19
    c: DistanceX(g-2,g1) = -25
    c: DistanceX(g-2,g0) = -25
    c: Equal(g2,g3)
    c: Diameter(g2) = 4
    c: Distance(g3,g2) = 19
FEATURE [Part::Extrusion] Extrude019
  Base = -> Sketch019
  Dir = (0,-1,2e-16)
  DirMode = 2
  FaceMakerClass = Part::FaceMakerBullseye
  LengthFwd = 10
  LengthRev = 0
  Solid = true
  Symmetric = true
FEATURE [Part::MultiFuse] Fusion015  label="HitPlankScrewHoles"
  Refine = true
  Shapes = -> [Extrude018,Extrude019,Extrude017]
FEATURE [Part::Cut] Cut009  label="Robot Body"
  Base = -> Fusion014
  Refine = true
  Tool = -> Fusion015
FEATURE [Sketcher::SketchObject] Sketch020
  FullyConstrained = true
  MapMode = 5
  Placement = pos=(0,5.9e-15,26.7549) rot=(1,0,0;3.14159rad)
  Support = -> [Cut009]
  sketch-geometry (4):
    g0: LineSegment StartX=36 StartY=10 StartZ=0 EndX=56 EndY=10 EndZ=0
    g1: LineSegment StartX=56 StartY=10 StartZ=0 EndX=56 EndY=8 EndZ=0
    g2: LineSegment StartX=56 StartY=8 StartZ=0 EndX=36 EndY=8 EndZ=0
    g3: LineSegment StartX=36 StartY=8 StartZ=0 EndX=36 EndY=10 EndZ=0
  constraints (12):
    c: Coincident(g0,g1)
    c: Coincident(g1,g2)
    c: Coincident(g2,g3)
    c: Coincident(g3,g0)
    c: Horizontal(g0)
    c: Horizontal(g2)
    c: Vertical(g1)
    c: Vertical(g3)
    c: DistanceY(g-1,g1) = 8
    c: DistanceY(g1,g1) = 2
    c: DistanceX(g2,g2) = 20
    c: DistanceX(g-2,g2) = 36
FEATURE [Part::Extrusion] Extrude020  label="Motor Holders Lid Slot"
  Base = -> Sketch020
  Dir = (0,-2e-16,-1)
  DirMode = 2
  FaceMakerClass = Part::FaceMakerBullseye
  LengthFwd = 2
  LengthRev = 0
  Placement = pos=(0,1,0) rot=(0,0,1;0rad)
  Solid = true
  Symmetric = false
  TaperAngle = -3
FEATURE [Part::Extrusion] Extrude021  label="Motor Holders Lid Slot001"
  Base = -> Sketch020
  Dir = (0,-2e-16,-1)
  DirMode = 2
  FaceMakerClass = Part::FaceMakerBullseye
  LengthFwd = 2
  LengthRev = 0
  Placement = pos=(-92,17,0) rot=(0,0,1;0rad)
  Solid = true
  Symmetric = false
  TaperAngle = -3
FEATURE [Part::Extrusion] Extrude022  label="Motor Holders Lid Slot002"
  Base = -> Sketch020
  Dir = (0,-2e-16,-1)
  DirMode = 2
  FaceMakerClass = Part::FaceMakerBullseye
  LengthFwd = 2
  LengthRev = 0
  Placement = pos=(0,17,0) rot=(0,0,1;0rad)
  Solid = true
  Symmetric = false
  TaperAngle = -3
FEATURE [Part::Extrusion] Extrude023  label="Motor Holders Lid Slot003"
  Base = -> Sketch020
  Dir = (0,-2e-16,-1)
  DirMode = 2
  FaceMakerClass = Part::FaceMakerBullseye
  LengthFwd = 2
  LengthRev = 0
  Placement = pos=(-92,1,0) rot=(0,0,1;0rad)
  Solid = true
  Symmetric = false
  TaperAngle = -3
FEATURE [Part::MultiFuse] Fusion016  label="Motor Lid Gaps"
  Refine = true
  Shapes = -> [Extrude020,Extrude021,Extrude022,Extrude023]
FEATURE [Part::Cut] Cut010
  Base = -> Cut009
  Refine = true
  Tool = -> Fusion016
FEATURE [Sketcher::SketchObject] Sketch021
  FullyConstrained = true
  MapMode = 5
  Placement = pos=(0,2.25e-14,31.7549) rot=(1,0,0;3.14159rad)
  Support = -> [Cut010]
  sketch-geometry (8):
    g0: LineSegment StartX=-70 StartY=-44.9 StartZ=0 EndX=-25 EndY=-44.9 EndZ=0
    g1: LineSegment StartX=-25 StartY=-44.9 StartZ=0 EndX=-25 EndY=-63.3 EndZ=0
    g2: LineSegment StartX=-25 StartY=-63.3 StartZ=0 EndX=-70 EndY=-63.3 EndZ=0
    g3: LineSegment StartX=-70 StartY=-63.3 StartZ=0 EndX=-70 EndY=-44.9 EndZ=0
    g4: LineSegment StartX=-72 StartY=-42.9 StartZ=0 EndX=-23 EndY=-42.9 EndZ=0
    g5: LineSegment StartX=-23 StartY=-42.9 StartZ=0 EndX=-23 EndY=-65.3 EndZ=0
    g6: LineSegment StartX=-23 StartY=-65.3 StartZ=0 EndX=-72 EndY=-65.3 EndZ=0
    g7: LineSegment StartX=-72 StartY=-65.3 StartZ=0 EndX=-72 EndY=-42.9 EndZ=0
  constraints (24):
    c: Coincident(g0,g1)
    c: Coincident(g1,g2)
    c: Coincident(g2,g3)
    c: Coincident(g3,g0)
    c: Horizontal(g0)
    c: Horizontal(g2)
    c: Vertical(g1)
    c: Vertical(g3)
    c: Coincident(g4,g5)
    c: Coincident(g5,g6)
    c: Coincident(g6,g7)
    c: Coincident(g7,g4)
    c: Horizontal(g4)
    c: Horizontal(g6)
    c: Vertical(g5)
    c: Vertical(g7)
    c: Distance(g1,g5) = 2
    c: Distance(g1,g6) = 2
    c: Distance(g0,g4) = 2
    c: DistanceY(g-1,g0) = -44.9
    c: DistanceX(g-2,g0) = -25
    c: DistanceX(g0,g0) = 45
    c: DistanceY(g1,g1) = 18.4
    c: Distance(g0,g7) = 2
FEATURE [Part::Extrusion] Extrude024  label="Arduino Walls"
  Base = -> Sketch021
  Dir = (0,-7e-16,-1)
  DirMode = 2
  FaceMakerClass = Part::FaceMakerBullseye
  LengthFwd = 10
  LengthRev = 0
  Placement = pos=(0,-108,-19) rot=(0,0,1;0rad)
  Solid = true
  Symmetric = false
FEATURE [Part::MultiFuse] Fusion017  label="Full Robot Body"
  Refine = true
  Shapes = -> [Cut010,Extrude024]
FEATURE [Sketcher::SketchObject] Sketch024
  FullyConstrained = false
  MapMode = 5
  Placement = pos=(0,0,2) rot=(0,0,1;0rad)
  Support = -> [Fusion017]
  sketch-geometry (2):
    g0: Circle CenterX=15.0092 CenterY=-109.45 CenterZ=0 NormalX=0 NormalY=0 NormalZ=1 AngleXU=0 Radius=1.75
    g1: Circle CenterX=-15.0092 CenterY=-109.45 CenterZ=0 NormalX=0 NormalY=0 NormalZ=1 AngleXU=0 Radius=1.75
  constraints (2):
    c: Diameter(g0) = 3.5
    c: Diameter(g1) = 3.5
FEATURE [Part::Extrusion] Extrude025  label="Idle Wheel Base Screw Hole"
  Base = -> Sketch024
  Dir = (0,0,1)
  DirMode = 2
  FaceMakerClass = Part::FaceMakerBullseye
  LengthFwd = 10
  LengthRev = 0
  Solid = true
  Symmetric = true
FEATURE [Part::Cut] Cut011
  Base = -> Fusion017
  Refine = true
  Tool = -> Extrude025
FEATURE [Part::MultiFuse] Fusion018  label="Full Robot Body001"
  Refine = true
  Shapes = -> [Cut011,Extrude026]
FEATURE [Sketcher::SketchObject] Sketch025
  FullyConstrained = false
  MapMode = 5
  Placement = pos=(0,0,35) rot=(0,0,1;0rad)
  Support = -> [Fusion018]
  sketch-geometry (21):
    g0: LineSegment StartX=-59.987 StartY=34.8273 StartZ=0 EndX=59.8041 EndY=34.8273 EndZ=0
    g1: LineSegment StartX=59.8041 StartY=34.8273 StartZ=0 EndX=59.8041 EndY=-34.9668 EndZ=0
    g2: LineSegment StartX=59.8041 StartY=-34.9668 StartZ=0 EndX=94.9993 EndY=-34.9668 EndZ=0
    g3: LineSegment StartX=94.9993 StartY=-34.9668 StartZ=0 EndX=94.9993 EndY=-89.9973 EndZ=0
    g4: LineSegment StartX=94.9993 StartY=-89.9973 StartZ=0 EndX=44.9644 EndY=-123.178 EndZ=0
    g5: LineSegment StartX=44.9644 StartY=-123.178 StartZ=0 EndX=-45.0068 EndY=-123.178 EndZ=0
    g6: LineSegment StartX=-45.0068 StartY=-123.178 StartZ=0 EndX=-94.9992 EndY=-90.0114 EndZ=0
    g7: LineSegment StartX=-94.9992 StartY=-90.0114 StartZ=0 EndX=-94.9992 EndY=-35.0079 EndZ=0
    g8: LineSegment StartX=-94.9992 StartY=-35.0079 StartZ=0 EndX=-59.987 EndY=-35.0079 EndZ=0
    g9: LineSegment StartX=-59.987 StartY=-35.0079 StartZ=0 EndX=-59.987 EndY=34.8273 EndZ=0
    g10: LineSegment StartX=-9.99147 StartY=-91.5603 StartZ=0 EndX=10.0409 EndY=-91.5603 EndZ=0
    g11: LineSegment StartX=10.0409 StartY=-91.5603 StartZ=0 EndX=10.0409 EndY=-95.508 EndZ=0
    g12: LineSegment StartX=10.0409 StartY=-95.508 StartZ=0 EndX=-9.99147 EndY=-95.508 EndZ=0
    g13: LineSegment StartX=-9.99147 StartY=-95.508 StartZ=0 EndX=-9.99147 EndY=-91.5603 EndZ=0
    g14: Circle CenterX=37.419 CenterY=29.3 CenterZ=0 NormalX=0 NormalY=0 NormalZ=1 AngleXU=0 Radius=1.5
    g15: Circle CenterX=-37.6122 CenterY=29.279 CenterZ=0 NormalX=0 NormalY=0 NormalZ=1 AngleXU=0 Radius=1.5
    g16: Circle CenterX=-0.59146 CenterY=-34.6907 CenterZ=0 NormalX=0 NormalY=0 NormalZ=1 AngleXU=0 Radius=1.5
    g17: Circle CenterX=70.9045 CenterY=-39.7106 CenterZ=0 NormalX=0 NormalY=0 NormalZ=1 AngleXU=0 Radius=1.5
    g18: Circle CenterX=30.5752 CenterY=-118.304 CenterZ=0 NormalX=0 NormalY=0 NormalZ=1 AngleXU=0 Radius=1.5
    g19: Circle CenterX=-31.3681 CenterY=-118.305 CenterZ=0 NormalX=0 NormalY=0 NormalZ=1 AngleXU=0 Radius=1.5
    g20: Circle CenterX=-67.5923 CenterY=-39.7098 CenterZ=0 NormalX=0 NormalY=0 NormalZ=1 AngleXU=0 Radius=1.5
  constraints (33):
    c: Horizontal(g0)
    c: Coincident(g0,g1)
    c: Vertical(g1)
    c: Coincident(g1,g2)
    c: Horizontal(g2)
    c: Coincident(g2,g3)
    c: Vertical(g3)
    c: Coincident(g3,g4)
    c: Coincident(g4,g5)
    c: Horizontal(g5)
    c: Coincident(g5,g6)
    c: Coincident(g6,g7)
    c: Vertical(g7)
    c: Coincident(g7,g8)
    c: Horizontal(g8)
    c: Coincident(g8,g9)
    c: Coincident(g9,g0)
    c: Vertical(g9)
    c: Coincident(g10,g11)
    c: Coincident(g11,g12)
    c: Coincident(g12,g13)
    c: Coincident(g13,g10)
    c: Horizontal(g10)
    c: Horizontal(g12)
    c: Vertical(g11)
    c: Vertical(g13)
    c: Diameter(g14) = 3
    c: Diameter(g15) = 3
    c: Diameter(g16) = 3
    c: Diameter(g17) = 3
    c: Diameter(g18) = 3
    c: Diameter(g19) = 3
    c: Diameter(g20) = 3
FEATURE [Part::Extrusion] Extrude027  label="Lid Base"
  Base = -> Sketch025
  Dir = (0,0,1)
  DirMode = 2
  FaceMakerClass = Part::FaceMakerBullseye
  LengthFwd = 3
  LengthRev = 0
  Solid = true
  Symmetric = false
FEATURE [Part::Fillet] Fillet
  Base = -> Extrude027
  Edges = 21 edges r=1: [Edge4,Edge7,Edge10,Edge13,Edge16,Edge19,Edge22,Edge25,Edge28,Edge30,Edge34,Edge37,Edge40,Edge42,Edge45,Edge48,Edge51,Edge54,Edge57,Edge60,Edge63]
FEATURE [Sketcher::SketchObject] Sketch026
  FullyConstrained = true
  MapMode = 5
  Placement = pos=(0,0,38) rot=(0,0,1;0rad)
  Support = -> [Fillet]
  sketch-geometry (1):
    g0: Circle CenterX=0 CenterY=-110 CenterZ=0 NormalX=0 NormalY=0 NormalZ=1 AngleXU=0 Radius=2
  constraints (3):
    c: Diameter(g0) = 4
    c: DistanceY(g0,g-1) = 110
    c: PointOnObject(g0,g-2)
FEATURE [Part::Extrusion] Extrude028  label="Weapon Wire slot"
  Base = -> Sketch026
  Dir = (0,0,1)
  DirMode = 2
  FaceMakerClass = Part::FaceMakerBullseye
  LengthFwd = 10
  LengthRev = 0
  Placement = pos=(-27,0,-6.5) rot=(0,0,1;0rad)
  Solid = true
  Symmetric = false
FEATURE [Part::Cut] Cut012
  Base = -> Fillet
  Refine = true
  Tool = -> Extrude028
FEATURE [Sketcher::SketchObject] Sketch028
  FullyConstrained = true
  MapMode = 5
  Placement = pos=(0,0,38) rot=(0,0,1;0rad)
  Support = -> [Cut012]
  sketch-geometry (9):
    g0: LineSegment StartX=-17 StartY=-100 StartZ=0 EndX=0 EndY=-100 EndZ=0
    g1: LineSegment StartX=0 StartY=-100 StartZ=0 EndX=0 EndY=-102 EndZ=0
    g2: LineSegment StartX=0 StartY=-102 StartZ=0 EndX=-17 EndY=-102 EndZ=0
    g3: LineSegment StartX=-17 StartY=-102 StartZ=0 EndX=-17 EndY=-100 EndZ=0
    g4: LineSegment StartX=-17 StartY=-118 StartZ=0 EndX=0 EndY=-118 EndZ=0
    g5: LineSegment StartX=0 StartY=-118 StartZ=0 EndX=0 EndY=-120 EndZ=0
    g6: LineSegment StartX=0 StartY=-120 StartZ=0 EndX=-17 EndY=-120 EndZ=0
    g7: LineSegment StartX=-17 StartY=-120 StartZ=0 EndX=-17 EndY=-118 EndZ=0
    g8: LineSegment StartX=0 StartY=-102 StartZ=0 EndX=0 EndY=-118 EndZ=0
  constraints (26):
    c: Coincident(g0,g1)
    c: Coincident(g1,g2)
    c: Coincident(g2,g3)
    c: Coincident(g3,g0)
    c: Horizontal(g2)
    c: Vertical(g1)
    c: Vertical(g3)
    c: Coincident(g4,g5)
    c: Coincident(g5,g6)
    c: Coincident(g6,g7)
    c: Coincident(g7,g4)
    c: Horizontal(g4)
    c: Horizontal(g6)
    c: Vertical(g5)
    c: Vertical(g7)
    c: Distance(g1,g4) = 16
    c: Distance(g-1,g0) = 100
    c: DistanceX(g0,g0) = 17
    c: DistanceY(g3,g3) = 2
    c: DistanceY(g5,g5) = 2
    c: DistanceX(g6,g6) = 17
    c: Coincident(g8,g1)
    c: Coincident(g8,g4)
    c: Vertical(g8)
    c: DistanceY(g1,g1) = 2
    c: PointOnObject(g0,g-2)
FEATURE [Part::Extrusion] Extrude029  label="Motor Flange Gap"
  Base = -> Sketch028
  Dir = (0,0,1)
  DirMode = 2
  FaceMakerClass = Part::FaceMakerBullseye
  LengthFwd = 10
  LengthRev = 0
  Solid = true
  Symmetric = true
FEATURE [Part::Cut] Cut013
  Base = -> Cut012
  Refine = true
  Tool = -> Extrude029
FEATURE [Part::Box] Box008  label="Cubo006"
  AttacherType = Attacher::AttachEngine3D
  Height = 35
  Length = 186
  Placement = pos=(-93,-147,1) rot=(0,0,1;0rad)
  Width = 4
FEATURE [Part::Box] Box009  label="Cubo007"
  AttacherType = Attacher::AttachEngine3D
  Height = 40
  Length = 200
  Placement = pos=(-100,-140,-4) rot=(0,0,1;0rad)
  Width = 50
FEATURE [Part::Cut] Cut015
  Base = -> Fusion018
  Tool = -> Box009
FEATURE [Sketcher::SketchObject] Sketch036
  FullyConstrained = false
  sketch-geometry (2):
    g0: ArcOfCircle CenterX=0.0180278 CenterY=37.967 CenterZ=0 NormalX=0 NormalY=0 NormalZ=1 AngleXU=0 Radius=158.19 StartAngle=4.08404 EndAngle=5.34074
    g1: LineSegment StartX=-92.9675 StartY=-90.0081 StartZ=0 EndX=93.0036 EndY=-90.0081 EndZ=0
  constraints (3):
    c: Coincident(g1,g0)
    c: Coincident(g1,g0)
    c: Horizontal(g1)
FEATURE [Part::Extrusion] Extrude034
  Base = -> Sketch036
  Dir = (0,0,1)
  DirMode = 2
  FaceMakerClass = Part::FaceMakerBullseye
  LengthFwd = 35
  LengthRev = 0
  Solid = true
  Symmetric = false
FEATURE [Part::Thickness] Thickness003
  Faces = -> Extrude034 [Face4]
  Intersection = false
  Join = 0
  Mode = 0
  Placement = pos=(0,-56,0) rot=(0,0,1;0rad)
  SelfIntersection = false
  Value = 2
FEATURE [Part::Cut] Cut
  Base = -> Thickness003
  Placement = pos=(0,56,2) rot=(0,0,1;0rad)
  Tool = -> Box008
FEATURE [Part::Box] Box  label="Cubo"
  AttacherType = Attacher::AttachEngine3D
  Height = 2
  Length = 200
  Placement = pos=(-101,-136,35) rot=(0,0,1;0rad)
  Width = 60
FEATURE [Part::Cut] Cut016
  Base = -> Cut
  Tool = -> Box
FEATURE [Part::Feature] Part__Feature046  label="Robot Rim"
  shape: bbox 40 x 40 x 20.01 mm, 43 faces (baked)
FEATURE [Part::Feature] Part__Feature047  label="Robot Slick Tire"
  Placement = pos=(0,0,10) rot=(0,0,1;0rad)
  shape: bbox 45 x 45 x 15 mm, 4 faces (baked)
FEATURE [App::Part] robot  label="LeftTire"
  Group = -> [Part__Feature046,Part__Feature047]
  Origin = -> Origin002
  Placement = pos=(61.5,0,7) rot=(0,1,0;1.5708rad)
FEATURE [Part::Feature] Part__Feature048  label="Robot Rim001"
  shape: bbox 40 x 40 x 20.01 mm, 43 faces (baked)
FEATURE [Part::Feature] Part__Feature049  label="Robot Slick Tire001"
  Placement = pos=(0,0,10) rot=(0,0,1;0rad)
  shape: bbox 45 x 45 x 15 mm, 4 faces (baked)
FEATURE [App::Part] robot001  label="RightTire"
  Group = -> [Part__Feature048,Part__Feature049]
  Origin = -> Origin003
  Placement = pos=(-62,0,7) rot=(0,1,0;4.71239rad)
FEATURE [Part::Feature] Part__Feature  label="L298N"
  Placement = pos=(21.5,29,6) rot=(1,0,0;1.5708rad)
  shape: bbox 43 x 43 x 25 mm, 410 faces (baked)
FEATURE [Part::Feature] Part__Feature001  label="Motor Case"
  shape: bbox 14 x 10 x 12 mm, 26 faces (baked)
FEATURE [Part::Feature] Part__Feature002  label="Rear Cover"
  Placement = pos=(7,0,0) rot=(0,0,1;0rad)
  shape: bbox 9 x 10 x 12 mm, 45 faces (baked)
FEATURE [Part::Feature] Part__Feature003  label="Rear Bearing"
  Placement = pos=(8.5,0,0) rot=(1,0,0;0.268142rad)
  shape: bbox 3 x 5 x 5 mm, 9 faces (baked)
FEATURE [Part::Feature] Part__Feature004  label="Front Bearing"
  Placement = pos=(-5.5,-1e-15,0) rot=(0,0,1;0rad)
  shape: bbox 1.5 x 4 x 4 mm, 6 faces (baked)
FEATURE [Part::Feature] Part__Feature005  label="Rotor"
  Placement = pos=(7,-3e-15,0) rot=(1,0,0;0.383419rad)
  shape: bbox 16.7 x 7.6 x 7.6 mm, 34 faces, 3 solids (baked)
FEATURE [Part::Feature] Part__Feature006  label="Spur 1-15_Spur01"
  Placement = pos=(-8.95,-3e-15,0) rot=(0.012886,0.999834,0.012886;1.57096rad)
  shape: bbox 1.5 x 3.391 x 3.382 mm, 38 faces (baked)
FEATURE [Part::Feature] Part__Feature007  label="Plate 1"
  Placement = pos=(-8,-6e-15,6e-15) rot=(0,1,0;1.5708rad)
  shape: bbox 1 x 10 x 12 mm, 14 faces (baked)
FEATURE [Part::Feature] Part__Feature008  label="Stand 2"
  Placement = pos=(-10,3.2,-3.6) rot=(0,0,1;0rad)
  shape: bbox 2 x 3 x 3 mm, 6 faces (baked)
FEATURE [Part::Feature] Part__Feature009  label="Stand 003"
  Placement = pos=(-10,-3.2,3.6) rot=(0,0,1;0rad)
  shape: bbox 2 x 3 x 3 mm, 6 faces (baked)
FEATURE [Part::Feature] Part__Feature010  label="Spur 2-24_Spur01"
  Placement = pos=(-8.95,2.21201,3.21201) rot=(0.153612,-0.976118,-0.153612;1.59497rad)
  shape: bbox 10.4 x 5.193 x 5.193 mm, 56 faces (baked)
FEATURE [Part::Feature] Part__Feature011  label="Plate 2"
  Placement = pos=(-11,-1.9e-14,5e-15) rot=(0,1,0;1.5708rad)
  shape: bbox 1 x 10 x 12 mm, 17 faces (baked)
FEATURE [Part::Feature] Part__Feature012  label="Spur 2-15_Spur01"
  Placement = pos=(-11.2,2.21201,3.21201) rot=(0.392285,0.832,0.392285;1.75369rad)
  shape: bbox 3 x 3.389 x 3.386 mm, 34 faces (baked)
FEATURE [Part::Feature] Part__Feature013  label="Spur 1-26_Spur01"
  Placement = pos=(-11.95,-0.153707,-0.136628) rot=(-0.467826,-0.749852,0.467826;1.85478rad)
  shape: bbox 4.2 x 5.587 x 5.6 mm, 60 faces (baked)
FEATURE [Part::Feature] Part__Feature014  label="Spur 1-15_Spur002"
  Placement = pos=(-13.45,-0.153707,-0.136628) rot=(-0.575214,0.581599,-0.575214;2.08803rad)
  shape: bbox 1.5 x 3.378 x 3.392 mm, 38 faces (baked)
FEATURE [Part::Feature] Part__Feature015  label="Stand 4"
  Placement = pos=(-16.1,3.2,-3.6) rot=(-1,0,0;1.00084rad)
  shape: bbox 5.1 x 3 x 3 mm, 6 faces (baked)
FEATURE [Part::Feature] Part__Feature016  label="Stand 004"
  Placement = pos=(-16.1,-3.2,3.6) rot=(1,0,0;1.52971rad)
  shape: bbox 5.1 x 3 x 3 mm, 6 faces (baked)
FEATURE [Part::Feature] Part__Feature017  label="Spur 1-24_Spur01"
  Placement = pos=(-13.45,-2.35559,-3.35559) rot=(-0.550538,0.627547,-0.550538;2.02074rad)
  shape: bbox 7.1 x 5.2 x 5.2 mm, 56 faces (baked)
FEATURE [Part::Feature] Part__Feature018  label="Plate 3"
  Placement = pos=(-16.1,-2.1e-14,5e-15) rot=(0.707107,0,-0.707107;3.14159rad)
  shape: bbox 2 x 10.2 x 12 mm, 29 faces (baked)
FEATURE [Part::Feature] Part__Feature019  label="Spur 1-15_Spur003"
  Placement = pos=(-15.15,-2.35559,-3.35559) rot=(0.659293,0.361476,0.659293;2.44787rad)
  shape: bbox 1.5 x 3.389 x 3.386 mm, 38 faces (baked)
FEATURE [Part::Feature] Part__Feature020  label="Spur 2-26_Spur01"
  Placement = pos=(-15.15,-2.7e-14,5e-15) rot=(0.080265,0.993537,0.080265;1.57728rad)
  shape: bbox 11.5 x 5.592 x 5.599 mm, 59 faces (baked)
FEATURE [Part::Feature] Part__Feature021  label="countersunk flat head cross recess screw_iso_ISO 7046-1 - M2 x 12 - Z --- 12N"
  Placement = pos=(-17.4,-3.2,3.6) rot=(1,0,0;0.036509rad)
  shape: bbox 12 x 3.8 x 3.8 mm, 41 faces (baked)
FEATURE [Part::Feature] Part__Feature022  label="countersunk flat head cross recess screw_iso_ISO 7046-1 - M2 x 12 - Z --- 12N001"
  Placement = pos=(-17.4,3.2,-3.6) rot=(1,0,0;1.44457rad)
  shape: bbox 12 x 3.8 x 3.8 mm, 41 faces (baked)
FEATURE [App::Part] GA12_N20_Motor_Complet  label="Left Motor"
  Group = -> [Part__Feature001,Part__Feature002,Part__Feature003,Part__Feature004,Part__Feature005,Part__Feature006,Part__Feature007,Part__Feature008,Part__Feature009,Part__Feature010,Part__Feature011,Part__Feature012,Part__Feature013,Part__Feature014,Part__Feature015,Part__Feature016,Part__Feature017,Part__Feature018,Part__Feature019,Part__Feature020,Part__Feature021,Part__Feature022]
  Origin = -> Origin
  Placement = pos=(40,-7.2e-15,7) rot=(0,0.707107,0.707107;3.14159rad)
FEATURE [Part::Feature] Part__Feature107  label="Motor Case001"
  shape: bbox 14 x 10 x 12 mm, 26 faces (baked)
FEATURE [Part::Feature] Part__Feature108  label="Rear Cover001"
  Placement = pos=(7,0,0) rot=(0,0,1;0rad)
  shape: bbox 9 x 10 x 12 mm, 45 faces (baked)
FEATURE [Part::Feature] Part__Feature109  label="Rear Bearing001"
  Placement = pos=(8.5,0,0) rot=(1,0,0;0.268142rad)
  shape: bbox 3 x 5 x 5 mm, 9 faces (baked)
FEATURE [Part::Feature] Part__Feature110  label="Front Bearing001"
  Placement = pos=(-5.5,-1e-15,0) rot=(0,0,1;0rad)
  shape: bbox 1.5 x 4 x 4 mm, 6 faces (baked)
FEATURE [Part::Feature] Part__Feature111  label="Rotor001"
  Placement = pos=(7,-3e-15,0) rot=(1,0,0;0.383419rad)
  shape: bbox 16.7 x 7.6 x 7.6 mm, 34 faces, 3 solids (baked)
FEATURE [Part::Feature] Part__Feature112  label="Spur 1-15_Spur004"
  Placement = pos=(-8.95,-3e-15,0) rot=(0.012886,0.999834,0.012886;1.57096rad)
  shape: bbox 1.5 x 3.391 x 3.382 mm, 38 faces (baked)
FEATURE [Part::Feature] Part__Feature113  label="Plate 004"
  Placement = pos=(-8,-6e-15,6e-15) rot=(0,1,0;1.5708rad)
  shape: bbox 1 x 10 x 12 mm, 14 faces (baked)
FEATURE [Part::Feature] Part__Feature114  label="Stand 005"
  Placement = pos=(-10,3.2,-3.6) rot=(0,0,1;0rad)
  shape: bbox 2 x 3 x 3 mm, 6 faces (baked)
FEATURE [Part::Feature] Part__Feature115  label="Stand 006"
  Placement = pos=(-10,-3.2,3.6) rot=(0,0,1;0rad)
  shape: bbox 2 x 3 x 3 mm, 6 faces (baked)
FEATURE [Part::Feature] Part__Feature116  label="Spur 2-24_Spur002"
  Placement = pos=(-8.95,2.21201,3.21201) rot=(0.153612,-0.976118,-0.153612;1.59497rad)
  shape: bbox 10.4 x 5.193 x 5.193 mm, 56 faces (baked)
FEATURE [Part::Feature] Part__Feature117  label="Plate 005"
  Placement = pos=(-11,-1.9e-14,5e-15) rot=(0,1,0;1.5708rad)
  shape: bbox 1 x 10 x 12 mm, 17 faces (baked)
FEATURE [Part::Feature] Part__Feature118  label="Spur 2-15_Spur002"
  Placement = pos=(-11.2,2.21201,3.21201) rot=(0.392285,0.832,0.392285;1.75369rad)
  shape: bbox 3 x 3.389 x 3.386 mm, 34 faces (baked)
FEATURE [Part::Feature] Part__Feature119  label="Spur 1-26_Spur002"
  Placement = pos=(-11.95,-0.153707,-0.136628) rot=(-0.467826,-0.749852,0.467826;1.85478rad)
  shape: bbox 4.2 x 5.587 x 5.6 mm, 60 faces (baked)
FEATURE [Part::Feature] Part__Feature120  label="Spur 1-15_Spur005"
  Placement = pos=(-13.45,-0.153707,-0.136628) rot=(-0.575214,0.581599,-0.575214;2.08803rad)
  shape: bbox 1.5 x 3.378 x 3.392 mm, 38 faces (baked)
FEATURE [Part::Feature] Part__Feature121  label="Stand 007"
  Placement = pos=(-16.1,3.2,-3.6) rot=(-1,0,0;1.00084rad)
  shape: bbox 5.1 x 3 x 3 mm, 6 faces (baked)
FEATURE [Part::Feature] Part__Feature122  label="Stand 008"
  Placement = pos=(-16.1,-3.2,3.6) rot=(1,0,0;1.52971rad)
  shape: bbox 5.1 x 3 x 3 mm, 6 faces (baked)
FEATURE [Part::Feature] Part__Feature123  label="Spur 1-24_Spur002"
  Placement = pos=(-13.45,-2.35559,-3.35559) rot=(-0.550538,0.627547,-0.550538;2.02074rad)
  shape: bbox 7.1 x 5.2 x 5.2 mm, 56 faces (baked)
FEATURE [Part::Feature] Part__Feature124  label="Plate 006"
  Placement = pos=(-16.1,-2.1e-14,5e-15) rot=(0.707107,0,-0.707107;3.14159rad)
  shape: bbox 2 x 10.2 x 12 mm, 29 faces (baked)
FEATURE [Part::Feature] Part__Feature125  label="Spur 1-15_Spur006"
  Placement = pos=(-15.15,-2.35559,-3.35559) rot=(0.659293,0.361476,0.659293;2.44787rad)
  shape: bbox 1.5 x 3.389 x 3.386 mm, 38 faces (baked)
FEATURE [Part::Feature] Part__Feature126  label="Spur 2-26_Spur002"
  Placement = pos=(-15.15,-2.7e-14,5e-15) rot=(0.080265,0.993537,0.080265;1.57728rad)
  shape: bbox 11.5 x 5.592 x 5.599 mm, 59 faces (baked)
FEATURE [Part::Feature] Part__Feature127  label="countersunk flat head cross recess screw_iso_ISO 7046-1 - M2 x 12 - Z --- 12N002"
  Placement = pos=(-17.4,-3.2,3.6) rot=(1,0,0;0.036509rad)
  shape: bbox 12 x 3.8 x 3.8 mm, 41 faces (baked)
FEATURE [Part::Feature] Part__Feature128  label="countersunk flat head cross recess screw_iso_ISO 7046-1 - M2 x 12 - Z --- 12N003"
  Placement = pos=(-17.4,3.2,-3.6) rot=(1,0,0;1.44457rad)
  shape: bbox 12 x 3.8 x 3.8 mm, 41 faces (baked)
FEATURE [App::Part] GA12_N20_Motor_Complet001  label="Left Motor001"
  Group = -> [Part__Feature107,Part__Feature108,Part__Feature109,Part__Feature110,Part__Feature111,Part__Feature112,Part__Feature113,Part__Feature114,Part__Feature115,Part__Feature116,Part__Feature117,Part__Feature118,Part__Feature119,Part__Feature120,Part__Feature121,Part__Feature122,Part__Feature123,Part__Feature124,Part__Feature125,Part__Feature126,Part__Feature127,Part__Feature128]
  Origin = -> Origin004
  Placement = pos=(40,-7.2e-15,7) rot=(0,0.707107,0.707107;3.14159rad)
FEATURE [Part::Feature] Part__Feature023  label="Motor Case002"
  shape: bbox 14 x 10 x 12 mm, 26 faces (baked)
FEATURE [Part::Feature] Part__Feature024  label="Rear Cover002"
  Placement = pos=(7,0,0) rot=(0,0,1;0rad)
  shape: bbox 9 x 10 x 12 mm, 45 faces (baked)
FEATURE [Part::Feature] Part__Feature025  label="Rear Bearing002"
  Placement = pos=(8.5,0,0) rot=(1,0,0;0.268142rad)
  shape: bbox 3 x 5 x 5 mm, 9 faces (baked)
FEATURE [Part::Feature] Part__Feature026  label="Front Bearing002"
  Placement = pos=(-5.5,-1e-15,0) rot=(0,0,1;0rad)
  shape: bbox 1.5 x 4 x 4 mm, 6 faces (baked)
FEATURE [Part::Feature] Part__Feature027  label="Rotor002"
  Placement = pos=(7,-3e-15,0) rot=(1,0,0;0.383419rad)
  shape: bbox 16.7 x 7.6 x 7.6 mm, 34 faces, 3 solids (baked)
FEATURE [Part::Feature] Part__Feature028  label="Spur 1-15_Spur007"
  Placement = pos=(-8.95,-3e-15,0) rot=(0.012886,0.999834,0.012886;1.57096rad)
  shape: bbox 1.5 x 3.391 x 3.382 mm, 38 faces (baked)
FEATURE [Part::Feature] Part__Feature029  label="Plate 007"
  Placement = pos=(-8,-6e-15,6e-15) rot=(0,1,0;1.5708rad)
  shape: bbox 1 x 10 x 12 mm, 14 faces (baked)
FEATURE [Part::Feature] Part__Feature030  label="Stand 009"
  Placement = pos=(-10,3.2,-3.6) rot=(0,0,1;0rad)
  shape: bbox 2 x 3 x 3 mm, 6 faces (baked)
FEATURE [Part::Feature] Part__Feature031  label="Stand 010"
  Placement = pos=(-10,-3.2,3.6) rot=(0,0,1;0rad)
  shape: bbox 2 x 3 x 3 mm, 6 faces (baked)
FEATURE [Part::Feature] Part__Feature032  label="Spur 2-24_Spur003"
  Placement = pos=(-8.95,2.21201,3.21201) rot=(0.153612,-0.976118,-0.153612;1.59497rad)
  shape: bbox 10.4 x 5.193 x 5.193 mm, 56 faces (baked)
FEATURE [Part::Feature] Part__Feature033  label="Plate 008"
  Placement = pos=(-11,-1.9e-14,5e-15) rot=(0,1,0;1.5708rad)
  shape: bbox 1 x 10 x 12 mm, 17 faces (baked)
FEATURE [Part::Feature] Part__Feature034  label="Spur 2-15_Spur003"
  Placement = pos=(-11.2,2.21201,3.21201) rot=(0.392285,0.832,0.392285;1.75369rad)
  shape: bbox 3 x 3.389 x 3.386 mm, 34 faces (baked)
FEATURE [Part::Feature] Part__Feature035  label="Spur 1-26_Spur003"
  Placement = pos=(-11.95,-0.153707,-0.136628) rot=(-0.467826,-0.749852,0.467826;1.85478rad)
  shape: bbox 4.2 x 5.587 x 5.6 mm, 60 faces (baked)
FEATURE [Part::Feature] Part__Feature036  label="Spur 1-15_Spur008"
  Placement = pos=(-13.45,-0.153707,-0.136628) rot=(-0.575214,0.581599,-0.575214;2.08803rad)
  shape: bbox 1.5 x 3.378 x 3.392 mm, 38 faces (baked)
FEATURE [Part::Feature] Part__Feature037  label="Stand 011"
  Placement = pos=(-16.1,3.2,-3.6) rot=(-1,0,0;1.00084rad)
  shape: bbox 5.1 x 3 x 3 mm, 6 faces (baked)
FEATURE [Part::Feature] Part__Feature038  label="Stand 012"
  Placement = pos=(-16.1,-3.2,3.6) rot=(1,0,0;1.52971rad)
  shape: bbox 5.1 x 3 x 3 mm, 6 faces (baked)
FEATURE [Part::Feature] Part__Feature039  label="Spur 1-24_Spur003"
  Placement = pos=(-13.45,-2.35559,-3.35559) rot=(-0.550538,0.627547,-0.550538;2.02074rad)
  shape: bbox 7.1 x 5.2 x 5.2 mm, 56 faces (baked)
FEATURE [Part::Feature] Part__Feature040  label="Plate 009"
  Placement = pos=(-16.1,-2.1e-14,5e-15) rot=(0.707107,0,-0.707107;3.14159rad)
  shape: bbox 2 x 10.2 x 12 mm, 29 faces (baked)
FEATURE [Part::Feature] Part__Feature041  label="Spur 1-15_Spur009"
  Placement = pos=(-15.15,-2.35559,-3.35559) rot=(0.659293,0.361476,0.659293;2.44787rad)
  shape: bbox 1.5 x 3.389 x 3.386 mm, 38 faces (baked)
FEATURE [Part::Feature] Part__Feature042  label="Spur 2-26_Spur003"
  Placement = pos=(-15.15,-2.7e-14,5e-15) rot=(0.080265,0.993537,0.080265;1.57728rad)
  shape: bbox 11.5 x 5.592 x 5.599 mm, 59 faces (baked)
FEATURE [Part::Feature] Part__Feature043  label="countersunk flat head cross recess screw_iso_ISO 7046-1 - M2 x 12 - Z --- 12N004"
  Placement = pos=(-17.4,-3.2,3.6) rot=(1,0,0;0.036509rad)
  shape: bbox 12 x 3.8 x 3.8 mm, 41 faces (baked)
FEATURE [Part::Feature] Part__Feature044  label="countersunk flat head cross recess screw_iso_ISO 7046-1 - M2 x 12 - Z --- 12N005"
  Placement = pos=(-17.4,3.2,-3.6) rot=(1,0,0;1.44457rad)
  shape: bbox 12 x 3.8 x 3.8 mm, 41 faces (baked)
FEATURE [App::Part] GA12_N20_Motor_Complet002  label="Right Motor"
  Group = -> [Part__Feature023,Part__Feature024,Part__Feature025,Part__Feature026,Part__Feature027,Part__Feature028,Part__Feature029,Part__Feature030,Part__Feature031,Part__Feature032,Part__Feature033,Part__Feature034,Part__Feature035,Part__Feature036,Part__Feature037,Part__Feature038,Part__Feature039,Part__Feature040,Part__Feature041,Part__Feature042,Part__Feature043,Part__Feature044]
  Origin = -> Origin001
  Placement = pos=(-40,-1.5e-14,7) rot=(1,0,0;1.5708rad)
FEATURE [Part::Feature] Part__Feature051  label="Arduino Nano"
  Placement = pos=(8.85506,11.9484,3.8e-15) rot=(0,0,1;0rad)
  shape: bbox 43.18 x 18 x 6.8 mm, 962 faces (baked)
FEATURE [Part::Feature] Part__Feature052  label="Mini USB"
  Placement = pos=(8.54506,19.5727,4.14) rot=(0,0,1;0rad)
  shape: bbox 9.5 x 9.7 x 3.9 mm, 197 faces (baked)
FEATURE [Part::Feature] Part__Feature053  label="ATMEGA328P-AU--3DModel-STEP-56544.step.STEP.STEP.STEP"
  Placement = pos=(2.81625,4.09996,0.676804) rot=(1,0,0;1.5708rad)
  shape: bbox 9 x 9 x 1.2 mm, 650 faces, 33 solids (baked)
FEATURE [App::Part] ATMEGA328P_AU_STEP  label="ATMEGA328P-AU.STEP"
  Group = -> [Part__Feature053]
  Origin = -> Origin005
  Placement = pos=(19.8219,24.4243,4.0882) rot=(0,0,1;3.92699rad)
FEATURE [Part::Feature] Part__Feature054  label="CSTCE Crystal"
  Placement = pos=(25.8562,23.1047,4.15) rot=(0,0,-1;0.785398rad)
  shape: bbox 3.182 x 3.182 x 0.71 mm, 47 faces (baked)
FEATURE [Part::Feature] Part__Feature055  label="2Pin Tactile Switch 6x3.6"
  Placement = pos=(30.7142,19.8184,4.14) rot=(0,0,1;1.5708rad)
  shape: bbox 3.633 x 7.9 x 2.2 mm, 48 faces (baked)
FEATURE [Part::Feature] Part__Feature056  label="0603 Resistor"
  Placement = pos=(34.4251,22.4184,4.14) rot=(0,0,1;0rad)
  shape: bbox 1.6 x 0.8 x 0.5 mm, 69 faces (baked)
FEATURE [Part::Feature] Part__Feature057  label="0603 Resistor001"
  Placement = pos=(34.4251,20.7184,4.14) rot=(0,0,1;0rad)
  shape: bbox 1.6 x 0.8 x 0.5 mm, 69 faces (baked)
FEATURE [Part::Feature] Part__Feature058  label="0603 Resistor002"
  Placement = pos=(34.4251,18.9184,4.14) rot=(0,0,1;0rad)
  shape: bbox 1.6 x 0.8 x 0.5 mm, 69 faces (baked)
FEATURE [Part::Feature] Part__Feature059  label="0603 Resistor003"
  Placement = pos=(34.4251,17.2184,4.14) rot=(0,0,1;0rad)
  shape: bbox 1.6 x 0.8 x 0.5 mm, 69 faces (baked)
FEATURE [Part::Feature] Part__Feature060  label="Blue LED"
  Placement = pos=(37.0251,22.4184,4.14) rot=(0,0,1;0rad)
  shape: bbox 1.6 x 0.8 x 0.6 mm, 19 faces (baked)
FEATURE [Part::Feature] Part__Feature061  label="Green LED"
  Placement = pos=(37.0251,20.7184,4.14) rot=(0,0,1;0rad)
  shape: bbox 1.6 x 0.8 x 0.6 mm, 19 faces (baked)
FEATURE [Part::Feature] Part__Feature062  label="Red LED"
  Placement = pos=(37.0251,18.9184,4.14) rot=(0,0,1;0rad)
  shape: bbox 1.6 x 0.8 x 0.6 mm, 19 faces (baked)
FEATURE [Part::Feature] Part__Feature063  label="Blue LED001"
  Placement = pos=(37.0251,17.2184,4.14) rot=(0,0,1;0rad)
  shape: bbox 1.6 x 0.8 x 0.6 mm, 19 faces (baked)
FEATURE [Part::Feature] Part__Feature064  label="Header 2x3"
  Placement = pos=(45.6765,17.0321,4.14) rot=(0,0,1;1.5708rad)
  shape: bbox 5.075 x 7.615 x 10 mm, 168 faces, 6 solids (baked)
FEATURE [Part::Feature] Part__Feature065  label="SOT89"
  Placement = pos=(38.4751,17.3184,0.94) rot=(0,0,1;1.5708rad)
  shape: bbox 7.1 x 6.5 x 1.6 mm, 80 faces (baked)
FEATURE [Part::Feature] Part__Feature066  label="1206 Tantalum"
  Placement = pos=(38.6251,22.3684,2.54) rot=(0,1,0;3.14159rad)
  shape: bbox 3.2 x 1.6 x 1.5 mm, 24 faces (baked)
FEATURE [Part::Feature] Part__Feature067  label="0603 Resistor004"
  Placement = pos=(38.4251,24.9684,2.54) rot=(0,1,0;3.14159rad)
  shape: bbox 1.6 x 0.8 x 0.5 mm, 69 faces (baked)
FEATURE [Part::Feature] Part__Feature068  label="0603 Capacitor"
  Placement = pos=(35.0338,14.4684,2.54) rot=(0,1,0;3.14159rad)
  shape: bbox 1.6 x 0.8 x 0.7 mm, 69 faces (baked)
FEATURE [Part::Feature] Part__Feature069  label="1206 Tantalum001"
  Placement = pos=(7.64506,24.3684,2.54) rot=(1,0,0;3.14159rad)
  shape: bbox 3.2 x 1.6 x 1.5 mm, 24 faces (baked)
FEATURE [Part::Feature] Part__Feature070  label="0603 Capacitor001"
  Placement = pos=(6.90589,22.4745,2.54) rot=(0,1,0;3.14159rad)
  shape: bbox 1.6 x 0.8 x 0.7 mm, 69 faces (baked)
FEATURE [Part::Feature] Part__Feature071  label="0603 Capacitor002"
  Placement = pos=(17.8451,14.0245,2.54) rot=(0,1,0;3.14159rad)
  shape: bbox 1.6 x 0.8 x 0.7 mm, 69 faces (baked)
FEATURE [Part::Feature] Part__Feature072  label="0603 Capacitor003"
  Placement = pos=(17.8451,15.0767,2.54) rot=(0,1,0;3.14159rad)
  shape: bbox 1.6 x 0.8 x 0.7 mm, 69 faces (baked)
FEATURE [Part::Feature] Part__Feature073  label="0603 Capacitor004"
  Placement = pos=(25.3451,21.2855,2.54) rot=(0,1,0;3.14159rad)
  shape: bbox 1.6 x 0.8 x 0.7 mm, 69 faces (baked)
FEATURE [Part::Feature] Part__Feature074  label="0603 Resistor005"
  Placement = pos=(23.8451,15.8601,2.54) rot=(0,1,0;3.14159rad)
  shape: bbox 1.6 x 0.8 x 0.5 mm, 69 faces (baked)
FEATURE [Part::Feature] Part__Feature075  label="0603 Resistor006"
  Placement = pos=(23.8451,14.4709,2.54) rot=(0,1,0;3.14159rad)
  shape: bbox 1.6 x 0.8 x 0.5 mm, 69 faces (baked)
FEATURE [Part::Feature] Part__Feature076  label="CSTCE Crystal001"
  Placement = pos=(13.1731,14.7184,2.53) rot=(0,1,0;3.14159rad)
  shape: bbox 3.2 x 1.35 x 0.71 mm, 47 faces (baked)
FEATURE [Part::Feature] Part__Feature077  label="SOIC16"
  Placement = pos=(16.6451,19.5642,2.54) rot=(0,1,0;3.14159rad)
  shape: bbox 10.2 x 6 x 1.5 mm, 154 faces (baked)
FEATURE [App::Part] Arduino_Nano  label="Arduino Nano001"
  Group = -> [Part__Feature051,Part__Feature052,ATMEGA328P_AU_STEP,Part__Feature054,Part__Feature055,Part__Feature056,Part__Feature057,Part__Feature058,Part__Feature059,Part__Feature060,Part__Feature061,Part__Feature062,Part__Feature063,Part__Feature064,Part__Feature065,Part__Feature066,Part__Feature067,Part__Feature068,Part__Feature069,Part__Feature070,Part__Feature071,Part__Feature072,Part__Feature073,+4 more]
  Origin = -> Origin006
  Placement = pos=(-73.5,-34.5,12.5) rot=(1,0,0;3.14159rad)
FEATURE [Part::Feature] Part__Feature078  label="Varsayılan"
  shape: bbox 42.6 x 16.1 x 5.9 mm, 343 faces, 7 solids (baked)
FEATURE [App::Part] f818e014b189db61e14b8aa713db12f520221103_1_5sl1wb  label="Bluetooth Module"
  Group = -> [Part__Feature078]
  Origin = -> Origin007
  Placement = pos=(-8,-91.75,41) rot=(-0.57735,-0.57735,0.57735;4.18879rad)
FEATURE [Mesh::Feature] Brilliant_Snicket__1_  label="Caster Marble Holder"
  Placement = pos=(-45,-110,4.88e-14) rot=(-1,0,0;3.14159rad)
FEATURE [Part::Sphere] Sphere  label="Marble"
  Angle1 = -90
  Angle2 = 90
  Angle3 = 360
  AttacherType = Attacher::AttachEngine3D
  Placement = pos=(0,-109.5,-9) rot=(0,0,1;0rad)
  Radius = 7.5
FEATURE [Part::Feature] Part__Feature045  label="INTERRUPTOR BASCULANTE"
  Placement = pos=(-83.5,-33.5,27) rot=(0.57735,-0.57735,-0.57735;4.18879rad)
  shape: bbox 15.1 x 17.9 x 10.42 mm, 555 faces, 4 solids (baked)
FEATURE [Part::Feature] Part__Feature088  label="Left Motor Lid"
  Placement = pos=(-56.5,0,2.5) rot=(0,0,1;0rad)
  shape: bbox 20 x 18 x 5.1 mm, 18 faces (baked)
FEATURE [Part::Feature] Part__Feature089  label="Right Motor Lid"
  Placement = pos=(36,0,2.5) rot=(0,0,1;0rad)
  shape: bbox 20 x 18 x 5.1 mm, 18 faces (baked)
FEATURE [Sketcher::SketchObject] Sketch037
  FullyConstrained = false
  sketch-geometry (43):
    g0: Circle CenterX=-84.0119 CenterY=-98.415 CenterZ=0 NormalX=0 NormalY=0 NormalZ=1 AngleXU=0 Radius=1
    g1: Circle CenterX=-71.6395 CenterY=-105.289 CenterZ=0 NormalX=0 NormalY=0 NormalZ=1 AngleXU=0 Radius=1
    g2: Circle CenterX=-64.6743 CenterY=-108.588 CenterZ=0 NormalX=0 NormalY=0 NormalZ=1 AngleXU=0 Radius=1
    g3: Circle CenterX=-54.9597 CenterY=-112.437 CenterZ=0 NormalX=0 NormalY=0 NormalZ=1 AngleXU=0 Radius=1
    g4: Circle CenterX=-46.7114 CenterY=-115.37 CenterZ=0 NormalX=0 NormalY=0 NormalZ=1 AngleXU=0 Radius=1
    g5: Circle CenterX=-37.8216 CenterY=-117.753 CenterZ=0 NormalX=0 NormalY=0 NormalZ=1 AngleXU=0 Radius=1
    g6: Circle CenterX=-29.4817 CenterY=-119.494 CenterZ=0 NormalX=0 NormalY=0 NormalZ=1 AngleXU=0 Radius=1
    g7: Circle CenterX=-15.3322 CenterY=-121.624 CenterZ=0 NormalX=0 NormalY=0 NormalZ=1 AngleXU=0 Radius=1
    g8: Circle CenterX=-5.70918 CenterY=-122.357 CenterZ=0 NormalX=0 NormalY=0 NormalZ=1 AngleXU=0 Radius=1
    g9: Circle CenterX=4.28038 CenterY=-122.357 CenterZ=0 NormalX=0 NormalY=0 NormalZ=1 AngleXU=0 Radius=1
    g10: Circle CenterX=14.9115 CenterY=-121.532 CenterZ=0 NormalX=0 NormalY=0 NormalZ=1 AngleXU=0 Radius=1
    g11: Circle CenterX=23.0681 CenterY=-120.524 CenterZ=0 NormalX=0 NormalY=0 NormalZ=1 AngleXU=0 Radius=1
    g12: Circle CenterX=32.5078 CenterY=-119.149 CenterZ=0 NormalX=0 NormalY=0 NormalZ=1 AngleXU=0 Radius=1
    g13: Circle CenterX=41.8558 CenterY=-116.689 CenterZ=0 NormalX=0 NormalY=0 NormalZ=1 AngleXU=0 Radius=1
    g14: Circle CenterX=49.5542 CenterY=-114.383 CenterZ=0 NormalX=0 NormalY=0 NormalZ=1 AngleXU=0 Radius=1
    g15: Circle CenterX=57.1609 CenterY=-111.817 CenterZ=0 NormalX=0 NormalY=0 NormalZ=1 AngleXU=0 Radius=1
    g16: Circle CenterX=63.2096 CenterY=-109.159 CenterZ=0 NormalX=0 NormalY=0 NormalZ=1 AngleXU=0 Radius=1
    g17: Circle CenterX=69.3538 CenterY=-106.481 CenterZ=0 NormalX=0 NormalY=0 NormalZ=1 AngleXU=0 Radius=1
    g18: Circle CenterX=75.1276 CenterY=-103.731 CenterZ=0 NormalX=0 NormalY=0 NormalZ=1 AngleXU=0 Radius=1
    g19: Circle CenterX=80.5348 CenterY=-100.615 CenterZ=0 NormalX=0 NormalY=0 NormalZ=1 AngleXU=0 Radius=1
    g20: Circle CenterX=84.2923 CenterY=-98.5073 CenterZ=0 NormalX=0 NormalY=0 NormalZ=1 AngleXU=0 Radius=1
    g21: LineSegment StartX=-84.0119 StartY=-98.415 StartZ=0 EndX=-71.6395 EndY=-105.289 EndZ=0
    g22: LineSegment StartX=-64.6743 StartY=-108.588 StartZ=0 EndX=-54.9597 EndY=-112.437 EndZ=0
    g23: LineSegment StartX=-46.7114 StartY=-115.37 StartZ=0 EndX=-37.8216 EndY=-117.753 EndZ=0
    g24: LineSegment StartX=-29.4817 StartY=-119.494 StartZ=0 EndX=-15.3322 EndY=-121.624 EndZ=0
    g25: LineSegment StartX=-5.70918 StartY=-122.357 StartZ=0 EndX=4.28038 EndY=-122.357 EndZ=0
    g26: LineSegment StartX=14.9115 StartY=-121.532 StartZ=0 EndX=23.0681 EndY=-120.524 EndZ=0
    g27: LineSegment StartX=32.5078 StartY=-119.149 StartZ=0 EndX=41.8558 EndY=-116.689 EndZ=0
    g28: LineSegment StartX=49.5542 StartY=-114.383 StartZ=0 EndX=57.1609 EndY=-111.817 EndZ=0
    g29: LineSegment StartX=63.2096 StartY=-109.159 StartZ=0 EndX=69.3538 EndY=-106.481 EndZ=0
    g30: LineSegment StartX=75.1276 StartY=-103.731 StartZ=0 EndX=80.5348 EndY=-100.615 EndZ=0
    g31: LineSegment StartX=-71.6395 StartY=-105.289 StartZ=0 EndX=-64.6743 EndY=-108.588 EndZ=0
    g32: LineSegment StartX=-54.9597 StartY=-112.437 StartZ=0 EndX=-46.7114 EndY=-115.37 EndZ=0
    g33: LineSegment StartX=-37.8216 StartY=-117.753 StartZ=0 EndX=-29.4817 EndY=-119.494 EndZ=0
    g34: LineSegment StartX=-15.2581 StartY=-121.831 StartZ=0 EndX=-15.3322 EndY=-121.624 EndZ=0
    g35: LineSegment StartX=-5.70918 StartY=-122.357 StartZ=0 EndX=-15.3322 EndY=-121.624 EndZ=0
    g36: LineSegment StartX=4.28038 StartY=-122.357 StartZ=0 EndX=14.9115 EndY=-121.532 EndZ=0
    g37: LineSegment StartX=23.0681 StartY=-120.524 StartZ=0 EndX=32.5078 EndY=-119.149 EndZ=0
    g38: LineSegment StartX=42.0827 StartY=-116.689 StartZ=0 EndX=41.8558 EndY=-116.689 EndZ=0
    g39: LineSegment StartX=49.5542 StartY=-114.383 StartZ=0 EndX=42.0827 EndY=-116.689 EndZ=0
    g40: LineSegment StartX=57.1609 StartY=-111.817 StartZ=0 EndX=63.2096 EndY=-109.159 EndZ=0
    g41: LineSegment StartX=69.3538 StartY=-106.481 StartZ=0 EndX=75.1276 EndY=-103.731 EndZ=0
    g42: LineSegment StartX=80.5348 StartY=-100.615 StartZ=0 EndX=84.2923 EndY=-98.5073 EndZ=0
  constraints (46):
    c: Weight(g0) = 1
    c: Equal(g0, g1-g20) x20
    c: Coincident(g21,g0)
    c: Coincident(g21,g1)
    c: Coincident(g22,g2)
    c: Coincident(g22,g3)
    c: Coincident(g23,g4)
    c: Coincident(g23,g5)
    c: Coincident(g24,g6)
    c: Coincident(g24,g7)
    c: Coincident(g25,g8)
    c: Coincident(g25,g9)
    c: Horizontal(g25)
    c: Coincident(g26,g10)
    c: Coincident(g26,g11)
    c: Coincident(g27,g12)
    c: Coincident(g27,g13)
    c: Coincident(g28,g14)
    c: Coincident(g28,g15)
    c: Coincident(g29,g16)
    c: Coincident(g29,g17)
    c: Coincident(g30,g18)
    c: Coincident(g30,g19)
    c: Coincident(g31,g21)
    c: Coincident(g31,g22)
    c: Coincident(g32,g22)
    c: Coincident(g32,g23)
    c: Coincident(g33,g23)
    c: Coincident(g33,g24)
    c: Coincident(g34,g24)
    c: Coincident(g35,g25)
    c: Coincident(g35,g24)
    c: Coincident(g36,g25)
    c: Coincident(g36,g26)
    c: Coincident(g37,g26)
    c: Coincident(g37,g27)
    c: Coincident(g38,g27)
    c: Horizontal(g38)
    c: Coincident(g39,g28)
    c: Coincident(g39,g38)
    c: Coincident(g40,g28)
    c: Coincident(g40,g29)
    c: Coincident(g41,g29)
    c: Coincident(g41,g30)
    c: Coincident(g42,g30)
    c: Coincident(g42,g20)
FEATURE [Part::Extrusion] Extrude
  Base = -> Sketch037
  Dir = (0,0,1)
  DirMode = 2
  FaceMakerClass = Part::FaceMakerBullseye
  LengthFwd = 28
  LengthRev = 0
  Placement = pos=(0,-32,0) rot=(0,0,1;0rad)
  Solid = false
  Symmetric = false
FEATURE [Part::Extrusion] Extrude036  label="Robot Front Hit Plank"
  Base = -> Extrude
  Dir = (0,1,0)
  DirMode = 0
  FaceMakerClass = Part::FaceMakerBullseye
  LengthFwd = 2
  LengthRev = 0
  Placement = pos=(0,30,4) rot=(0,0,1;0rad)
  Solid = false
  Symmetric = false
FEATURE [Part::Feature] Part__Feature129  label="Bluetooth Module Holder001"
  Placement = pos=(0,1.5,0) rot=(0,0,1;0rad)
  shape: bbox 20 x 4 x 33 mm, 10 faces (baked)
FEATURE [Part::MultiFuse] Fusion
  Refine = true
  Shapes = -> [Cut015,Part__Feature129]
FEATURE [Part::MultiFuse] Fusion019  label="Full Robot Body002"
  Refine = true
  Shapes = -> [Cut016,Fusion]
FEATURE [Sketcher::SketchObject] Sketch038
  FullyConstrained = false
  MapMode = 5
  Placement = pos=(5.67e-13,3.818e-13,35) rot=(0,0,1;0rad)
  Support = -> [Fusion019]
  sketch-geometry (8):
    g0: LineSegment StartX=8 StartY=-91 StartZ=0 EndX=8.5 EndY=-91 EndZ=0
    g1: LineSegment StartX=8.5 StartY=-91 StartZ=0 EndX=8.5 EndY=-93.2 EndZ=0
    g2: LineSegment StartX=8.5 StartY=-93.2 StartZ=0 EndX=8 EndY=-93.2 EndZ=0
    g3: LineSegment StartX=8 StartY=-93.2 StartZ=0 EndX=8 EndY=-91 EndZ=0
    g4: LineSegment StartX=-8 StartY=-91 StartZ=0 EndX=-8.5 EndY=-91 EndZ=0
    g5: LineSegment StartX=-8.5 StartY=-91 StartZ=0 EndX=-8.5 EndY=-93.2 EndZ=0
    g6: LineSegment StartX=-8.5 StartY=-93.2 StartZ=0 EndX=-8 EndY=-93.2 EndZ=0
    g7: LineSegment StartX=-8 StartY=-93.2 StartZ=0 EndX=-8 EndY=-91 EndZ=0
  constraints (20):
    c: Coincident(g0,g1)
    c: Coincident(g1,g2)
    c: Coincident(g2,g3)
    c: Coincident(g3,g0)
    c: Horizontal(g0)
    c: Horizontal(g2)
    c: Vertical(g1)
    c: Vertical(g3)
    c: DistanceY(g1,g1) = 2.2
    c: DistanceX(g0,g0) = 0.5
    c: DistanceX(g-2,g0) = 8
    c: DistanceY(g-1,g0) = -91
    c: Coincident(g4,g5)
    c: Coincident(g5,g6)
    c: Coincident(g6,g7)
    c: Coincident(g7,g4)
    c: Horizontal(g4)
    c: Horizontal(g6)
    c: Vertical(g5)
    c: Vertical(g7)
FEATURE [Part::Extrusion] Extrude037
  Base = -> Sketch038
  Dir = (1.62e-14,1.09e-14,1)
  DirMode = 2
  FaceMakerClass = Part::FaceMakerBullseye
  LengthFwd = -32
  LengthRev = 0
  Solid = true
  Symmetric = false
FEATURE [Part::Cut] Cut017
  Base = -> Fusion019
  Refine = true
  Tool = -> Extrude037
FEATURE [Sketcher::SketchObject] Sketch039
  FullyConstrained = false
  MapMode = 5
  Placement = pos=(0,0,0) rot=(1,0,0;3.14159rad)
  Support = -> [Cut017]
  sketch-geometry (2):
    g0: Circle CenterX=15.0302 CenterY=109.419 CenterZ=0 NormalX=0 NormalY=0 NormalZ=1 AngleXU=0 Radius=1.75
    g1: Circle CenterX=-15.0302 CenterY=109.419 CenterZ=0 NormalX=0 NormalY=0 NormalZ=1 AngleXU=0 Radius=1.75
  constraints (2):
    c: Diameter(g0) = 3.5
    c: Diameter(g1) = 3.5
FEATURE [Part::Extrusion] Extrude038
  Base = -> Sketch039
  Dir = (0,0,-1)
  DirMode = 2
  FaceMakerClass = Part::FaceMakerBullseye
  LengthFwd = 10
  LengthRev = 0
  Solid = true
  Symmetric = true
FEATURE [Part::Cut] Cut018
  Base = -> Cut017
  Refine = true
  Tool = -> Extrude038
FEATURE [Sketcher::SketchObject] Sketch040
  FullyConstrained = false
  MapMode = 5
  Placement = pos=(0,0,35) rot=(0,0,1;0rad)
  Support = -> [Cut018]
  sketch-geometry (19):
    g0: LineSegment StartX=-60 StartY=35.0902 StartZ=0 EndX=60 EndY=35.0902 EndZ=0
    g1: LineSegment StartX=60 StartY=35.0902 StartZ=0 EndX=60 EndY=-34.9098 EndZ=0
    g2: LineSegment StartX=60 StartY=-34.9098 StartZ=0 EndX=95 EndY=-34.9098 EndZ=0
    g3: LineSegment StartX=95 StartY=-34.9098 StartZ=0 EndX=95 EndY=-89.9098 EndZ=0
    g4: LineSegment StartX=-60 StartY=35.0902 StartZ=0 EndX=-60 EndY=-34.9098 EndZ=0
    g5: LineSegment StartX=-60 StartY=-34.9098 StartZ=0 EndX=-95 EndY=-34.9098 EndZ=0
    g6: LineSegment StartX=-95 StartY=-34.9098 StartZ=0 EndX=-95 EndY=-89.9098 EndZ=0
    g7: ArcOfCircle CenterX=0 CenterY=35.7609 CenterZ=0 NormalX=0 NormalY=0 NormalZ=1 AngleXU=0 Radius=157.538 StartAngle=4.06509 EndAngle=5.35968
    g8: LineSegment StartX=-9.19712 StartY=-90.0815 StartZ=0 EndX=10.8029 EndY=-90.0815 EndZ=0
    g9: LineSegment StartX=10.8029 StartY=-90.0815 StartZ=0 EndX=10.8029 EndY=-94.0815 EndZ=0
    g10: LineSegment StartX=10.8029 StartY=-94.0815 StartZ=0 EndX=-9.19712 EndY=-94.0815 EndZ=0
    g11: LineSegment StartX=-9.19712 StartY=-94.0815 StartZ=0 EndX=-9.19712 EndY=-90.0815 EndZ=0
    g12: Circle CenterX=70.8984 CenterY=-39.7159 CenterZ=0 NormalX=0 NormalY=0 NormalZ=1 AngleXU=0 Radius=1.5
    g13: Circle CenterX=37.3895 CenterY=29.2909 CenterZ=0 NormalX=0 NormalY=0 NormalZ=1 AngleXU=0 Radius=1.5
    g14: Circle CenterX=-37.6063 CenterY=29.3041 CenterZ=0 NormalX=0 NormalY=0 NormalZ=1 AngleXU=0 Radius=1.5
    g15: Circle CenterX=-67.6186 CenterY=-39.6843 CenterZ=0 NormalX=0 NormalY=0 NormalZ=1 AngleXU=0 Radius=1.5
    g16: Circle CenterX=-0.618404 CenterY=-34.7081 CenterZ=0 NormalX=0 NormalY=0 NormalZ=1 AngleXU=0 Radius=1.5
    g17: Circle CenterX=2.48362 CenterY=-40.2556 CenterZ=0 NormalX=0 NormalY=0 NormalZ=1 AngleXU=0 Radius=1.5
    g18: Circle CenterX=2.50933 CenterY=-62.2942 CenterZ=0 NormalX=0 NormalY=0 NormalZ=1 AngleXU=0 Radius=1.5
  constraints (40):
    c: Horizontal(g0)
    c: Coincident(g0,g1)
    c: Vertical(g1)
    c: Coincident(g1,g2)
    c: Horizontal(g2)
    c: Coincident(g2,g3)
    c: Vertical(g3)
    c: Coincident(g0,g4)
    c: Vertical(g4)
    c: Coincident(g4,g5)
    c: Horizontal(g5)
    c: Coincident(g5,g6)
    c: Vertical(g6)
    c: DistanceX(g0,g0) = 120
    c: DistanceY(g1,g1) = 70
    c: Equal(g1,g4)
    c: DistanceX(g2,g2) = 35
    c: Equal(g2,g5)
    c: PointOnObject(g7,g-2)
    c: Coincident(g7,g6)
    c: Coincident(g7,g3)
    c: Equal(g3,g6)
    c: DistanceY(g3,g3) = 55
    c: Coincident(g8,g9)
    c: Coincident(g9,g10)
    c: Coincident(g10,g11)
    c: Coincident(g11,g8)
    c: Horizontal(g8)
    c: Horizontal(g10)
    c: Vertical(g9)
    c: Vertical(g11)
    c: DistanceX(g8,g8) = 20
    c: DistanceY(g9,g9) = 4
    c: Diameter(g12) = 3
    c: Diameter(g13) = 3
    c: Diameter(g14) = 3
    c: Diameter(g15) = 3
    c: Diameter(g16) = 3
    c: Diameter(g17) = 3
    c: Diameter(g18) = 3
FEATURE [Part::Extrusion] Extrude039  label="Robot Lid"
  Base = -> Sketch040
  Dir = (0,0,1)
  DirMode = 2
  FaceMakerClass = Part::FaceMakerBullseye
  LengthFwd = 2
  LengthRev = 0
  Solid = true
  Symmetric = false
FEATURE [Part::Feature] Part__Feature131  label="MG90servo_shaft"
  Placement = pos=(16.5,28.5,-6.25) rot=(0,-1,0;0.664889rad)
  shape: bbox 5 x 4.3 x 5 mm, 110 faces (baked)
FEATURE [Part::Feature] Part__Feature133  label="BAttery"
  Placement = pos=(0,-59.5,2) rot=(0,0,1;0rad)
  shape: bbox 23 x 53 x 10 mm, 8 faces (baked)
FEATURE [Sketcher::SketchObject] Sketch041
  FullyConstrained = false
  MapMode = 5
  Placement = pos=(5.67e-13,3.818e-13,35) rot=(0,0,1;0rad)
  Support = -> [Cut018]
  sketch-geometry (8):
    g0: LineSegment StartX=9.30818 StartY=-44.7647 StartZ=0 EndX=11.5082 EndY=-44.7647 EndZ=0
    g1: LineSegment StartX=11.5082 StartY=-44.7647 StartZ=0 EndX=11.5082 EndY=-57.7647 EndZ=0
    g2: LineSegment StartX=11.5082 StartY=-57.7647 StartZ=0 EndX=9.30818 EndY=-57.7647 EndZ=0
    g3: LineSegment StartX=9.30818 StartY=-57.7647 StartZ=0 EndX=9.30818 EndY=-44.7647 EndZ=0
    g4: LineSegment StartX=-9.30818 StartY=-44.7647 StartZ=0 EndX=-11.5082 EndY=-44.7647 EndZ=0
    g5: LineSegment StartX=-11.5082 StartY=-44.7647 StartZ=0 EndX=-11.5082 EndY=-57.7647 EndZ=0
    g6: LineSegment StartX=-11.5082 StartY=-57.7647 StartZ=0 EndX=-9.30818 EndY=-57.7647 EndZ=0
    g7: LineSegment StartX=-9.30818 StartY=-57.7647 StartZ=0 EndX=-9.30818 EndY=-44.7647 EndZ=0
  constraints (18):
    c: Coincident(g0,g1)
    c: Coincident(g1,g2)
    c: Coincident(g2,g3)
    c: Coincident(g3,g0)
    c: Horizontal(g0)
    c: Horizontal(g2)
    c: Vertical(g1)
    c: Vertical(g3)
    c: DistanceX(g2,g2) = 2.2
    c: DistanceY(g1,g1) = 13
    c: Coincident(g4,g5)
    c: Coincident(g5,g6)
    c: Coincident(g6,g7)
    c: Coincident(g7,g4)
    c: Horizontal(g4)
    c: Horizontal(g6)
    c: Vertical(g5)
    c: Vertical(g7)
FEATURE [Part::Extrusion] Extrude040  label="Weapon Servo Slotter"
  Base = -> Sketch041
  Dir = (1.62e-14,1.09e-14,1)
  DirMode = 2
  FaceMakerClass = Part::FaceMakerBullseye
  LengthFwd = -27
  LengthRev = 0
  Solid = true
  Symmetric = false
FEATURE [Part::Cut] Cut019
  Base = -> Cut018
  Refine = true
  Tool = -> Extrude040
FEATURE [Sketcher::SketchObject] Sketch042
  FullyConstrained = false
  MapMode = 5
  Placement = pos=(-14.5,0,0) rot=(0.57735,-0.57735,-0.57735;2.0944rad)
  Support = -> [Cut019]
  sketch-geometry (4):
    g0: LineSegment StartX=44.5722 StartY=16.4536 StartZ=0 EndX=57.5722 EndY=16.4536 EndZ=0
    g1: LineSegment StartX=57.5722 StartY=16.4536 StartZ=0 EndX=57.5722 EndY=12.4536 EndZ=0
    g2: LineSegment StartX=57.5722 StartY=12.4536 StartZ=0 EndX=44.5722 EndY=12.4536 EndZ=0
    g3: LineSegment StartX=44.5722 StartY=12.4536 StartZ=0 EndX=44.5722 EndY=16.4536 EndZ=0
  constraints (10):
    c: Coincident(g0,g1)
    c: Coincident(g1,g2)
    c: Coincident(g2,g3)
    c: Coincident(g3,g0)
    c: Horizontal(g0)
    c: Horizontal(g2)
    c: Vertical(g1)
    c: Vertical(g3)
    c: DistanceX(g0,g0) = 13
    c: DistanceY(g1,g1) = 4
FEATURE [Part::Extrusion] Extrude041  label="Servo Wire Gap"
  Base = -> Sketch042
  Dir = (-1,0,0)
  DirMode = 2
  FaceMakerClass = Part::FaceMakerBullseye
  LengthFwd = 10
  LengthRev = 0
  Solid = true
  Symmetric = true
FEATURE [Part::Cut] Cut020
  Base = -> Cut019
  Refine = true
  Tool = -> Extrude041
FEATURE [Sketcher::SketchObject] Sketch043
  FullyConstrained = false
  MapMode = 5
  Placement = pos=(5.67e-13,3.818e-13,35) rot=(0,0,1;0rad)
  Support = -> [Cut020]
  sketch-geometry (2):
    g0: Circle CenterX=-13.6003 CenterY=-51.262 CenterZ=0 NormalX=0 NormalY=0 NormalZ=1 AngleXU=0 Radius=1
    g1: Circle CenterX=13.6003 CenterY=-51.262 CenterZ=0 NormalX=0 NormalY=0 NormalZ=1 AngleXU=0 Radius=1
  constraints (2):
    c: Diameter(g0) = 2
    c: Diameter(g1) = 2
FEATURE [Part::Extrusion] Extrude042  label="Servo Screw Guide"
  Base = -> Sketch043
  Dir = (1.62e-14,1.09e-14,1)
  DirMode = 2
  FaceMakerClass = Part::FaceMakerBullseye
  LengthFwd = -15
  LengthRev = 0
  Solid = true
  Symmetric = false
FEATURE [Part::Cut] Cut021  label="Robot Full Body"
  Base = -> Cut020
  Refine = true
  Tool = -> Extrude042
FEATURE [Sketcher::SketchObject] Sketch044
  FullyConstrained = false
  MapMode = 5
  Placement = pos=(0,0,38) rot=(0,0,1;0rad)
  Support = -> [Cut013]
  sketch-geometry (4):
    g0: LineSegment StartX=-23 StartY=-44.514 StartZ=0 EndX=12 EndY=-44.514 EndZ=0
    g1: LineSegment StartX=12 StartY=-44.514 StartZ=0 EndX=12 EndY=-58.014 EndZ=0
    g2: LineSegment StartX=12 StartY=-58.014 StartZ=0 EndX=-23 EndY=-58.014 EndZ=0
    g3: LineSegment StartX=-23 StartY=-58.014 StartZ=0 EndX=-23 EndY=-44.514 EndZ=0
  constraints (11):
    c: Coincident(g0,g1)
    c: Coincident(g1,g2)
    c: Coincident(g2,g3)
    c: Coincident(g3,g0)
    c: Horizontal(g0)
    c: Horizontal(g2)
    c: Vertical(g1)
    c: Vertical(g3)
    c: DistanceX(g0,g0) = 35
    c: DistanceY(g1,g1) = 13.5
    c: DistanceX(g-1,g1) = 12
FEATURE [Part::Extrusion] Extrude043  label="Servo Lid Gap"
  Base = -> Sketch044
  Dir = (0,0,1)
  DirMode = 2
  FaceMakerClass = Part::FaceMakerBullseye
  LengthFwd = 30
  LengthRev = 0
  Placement = pos=(0.25,0,0) rot=(0,0,1;0rad)
  Solid = true
  Symmetric = true
FEATURE [Part::Cut] Cut022
  Base = -> Extrude039
  Refine = true
  Tool = -> Extrude043
FEATURE [Sketcher::SketchObject] Sketch
  FullyConstrained = false
  MapMode = 5
  Placement = pos=(5.67e-13,3.818e-13,35) rot=(0,0,1;0rad)
  Support = -> [Cut021]
  sketch-geometry (4):
    g0: LineSegment StartX=-16.778 StartY=-44.4921 StartZ=0 EndX=16.4262 EndY=-44.4921 EndZ=0
    g1: LineSegment StartX=16.4262 StartY=-44.4921 StartZ=0 EndX=16.4262 EndY=-57.8256 EndZ=0
    g2: LineSegment StartX=16.4262 StartY=-57.8256 StartZ=0 EndX=-16.778 EndY=-57.8256 EndZ=0
    g3: LineSegment StartX=-16.778 StartY=-57.8256 StartZ=0 EndX=-16.778 EndY=-44.4921 EndZ=0
  constraints (8):
    c: Coincident(g0,g1)
    c: Coincident(g1,g2)
    c: Coincident(g2,g3)
    c: Coincident(g3,g0)
    c: Horizontal(g0)
    c: Horizontal(g2)
    c: Vertical(g1)
    c: Vertical(g3)
FEATURE [Part::Extrusion] Extrude044  label="Battery Walls Servo Gap"
  Base = -> Sketch
  Dir = (1.62e-14,1.09e-14,1)
  DirMode = 2
  FaceMakerClass = Part::FaceMakerBullseye
  LengthFwd = -5
  LengthRev = 0
  Solid = true
  Symmetric = false
FEATURE [Part::Cut] Cut023  label="Body001"
  Base = -> Cut021
  Refine = true
  Tool = -> Extrude044
FEATURE [Sketcher::SketchObject] Sketch053
  FullyConstrained = false
  sketch-geometry (10):
    g0: LineSegment StartX=-48.1822 StartY=-117.243 StartZ=0 EndX=-37.0056 EndY=-120.416 EndZ=0
    g1: LineSegment StartX=-29.0026 StartY=-121.796 StartZ=0 EndX=-37.0056 EndY=-120.416 EndZ=0
    g2: LineSegment StartX=-29.0026 StartY=-121.796 StartZ=0 EndX=-16.4463 EndY=-123.728 EndZ=0
    g3: LineSegment StartX=-16.4463 StartY=-123.728 StartZ=0 EndX=-5.13172 EndY=-124.556 EndZ=0
    g4: LineSegment StartX=-5.13172 StartY=-124.556 StartZ=0 EndX=4.38905 EndY=-124.556 EndZ=0
    g5: LineSegment StartX=4.38905 StartY=-124.556 StartZ=0 EndX=13.7718 EndY=-123.866 EndZ=0
    g6: LineSegment StartX=13.7718 StartY=-123.866 StartZ=0 EndX=22.6027 EndY=-122.9 EndZ=0
    g7: LineSegment StartX=22.6027 StartY=-122.9 StartZ=0 EndX=30.4677 EndY=-121.658 EndZ=0
    g8: LineSegment StartX=30.4677 StartY=-121.658 StartZ=0 EndX=37.7807 EndY=-120.002 EndZ=0
    g9: LineSegment StartX=37.7807 StartY=-120.002 StartZ=0 EndX=46.7496 EndY=-117.657 EndZ=0
  constraints (4):
    c: Coincident(g1,g0)
    c: Coincident(g2,g1)
    c: Coincident(g3,g2)
    c: Horizontal(g4)
FEATURE [Part::Extrusion] Extrude054
  Base = -> Sketch053
  Dir = (0,0,1)
  DirMode = 2
  FaceMakerClass = Part::FaceMakerBullseye
  LengthFwd = 23
  LengthRev = 0
  Solid = false
  Symmetric = false
FEATURE [Part::Extrusion] Extrude057  label="Front Hit Plank 2"
  Base = -> Extrude054
  Dir = (0,1,0)
  DirMode = 0
  FaceMakerClass = Part::FaceMakerBullseye
  LengthFwd = -1
  LengthRev = 0
  Placement = pos=(0,0.25,6) rot=(0,0,1;0rad)
  Solid = false
  Symmetric = false
FEATURE [Part::Feature] Part__Feature130  label="MG90servo_body"
  shape: bbox 32.05 x 28.5 x 13.53 mm, 90 faces (baked)
FEATURE [App::Part] MG90servo_assembly
  Group = -> [Part__Feature130,Part__Feature131]
  Origin = -> Origin008
  Placement = pos=(11.5,-57.5,22) rot=(0.57735,-0.57735,0.57735;2.0944rad)
FEATURE [Mesh::Feature] Powerful_Trug__4_  label="Axe"
  Placement = pos=(-18,-80.9196,46.9112) rot=(0.705758,-0.061746,-0.705758;3.01826rad)
FEATURE [Sketcher::SketchObject] Sketch054
  FullyConstrained = false
  MapMode = 5
  Placement = pos=(66.5738,-109.804,4) rot=(0.952554,0.215221,0.215221;1.61939rad)
  Support = -> [Extrude036]
  sketch-geometry (1):
    g0: Circle CenterX=0 CenterY=19.7495 CenterZ=0 NormalX=0 NormalY=0 NormalZ=1 AngleXU=0 Radius=2
  constraints (2):
    c: PointOnObject(g0,g-2)
    c: Diameter(g0) = 4
FEATURE [Part::Extrusion] Extrude058
  Base = -> Sketch054
  Dir = (0.429935,-0.90286,-6e-16)
  DirMode = 2
  FaceMakerClass = Part::FaceMakerBullseye
  LengthFwd = 10
  LengthRev = 0
  Solid = true
  Symmetric = true
FEATURE [Part::Extrusion] Extrude059
  Base = -> Sketch054
  Dir = (0.429935,-0.90286,-6e-16)
  DirMode = 2
  FaceMakerClass = Part::FaceMakerBullseye
  LengthFwd = 10
  LengthRev = 0
  Placement = pos=(0,0,-13) rot=(0,0,1;0rad)
  Solid = true
  Symmetric = true
FEATURE [Sketcher::SketchObject] Sketch055
  FullyConstrained = false
  MapMode = 5
  Placement = pos=(32.0395,-122.254,6) rot=(0.98386,0.126531,0.126531;1.58707rad)
  Support = -> [Extrude057]
  sketch-geometry (2):
    g0: Circle CenterX=0 CenterY=17.6116 CenterZ=0 NormalX=0 NormalY=0 NormalZ=1 AngleXU=0 Radius=2
    g1: Circle CenterX=0 CenterY=5.94641 CenterZ=0 NormalX=0 NormalY=0 NormalZ=1 AngleXU=0 Radius=2
  constraints (4):
    c: PointOnObject(g0,g-2)
    c: Diameter(g0) = 4
    c: PointOnObject(g1,g-2)
    c: Diameter(g1) = 4
FEATURE [Part::Extrusion] Extrude060
  Base = -> Sketch055
  Dir = (0.253028,-0.967459,2e-16)
  DirMode = 2
  FaceMakerClass = Part::FaceMakerBullseye
  LengthFwd = 15
  LengthRev = 0
  Solid = true
  Symmetric = true
FEATURE [Sketcher::SketchObject] Sketch056
  FullyConstrained = false
  MapMode = 5
  Placement = pos=(-34.665,-121.831,6) rot=(0.981163,-0.136601,-0.136601;1.58981rad)
  Support = -> [Extrude057]
  sketch-geometry (2):
    g0: Circle CenterX=0 CenterY=18.3678 CenterZ=0 NormalX=0 NormalY=0 NormalZ=1 AngleXU=0 Radius=2
    g1: Circle CenterX=0 CenterY=6.57646 CenterZ=0 NormalX=0 NormalY=0 NormalZ=1 AngleXU=0 Radius=2
  constraints (4):
    c: PointOnObject(g0,g-2)
    c: PointOnObject(g1,g-2)
    c: Diameter(g1) = 4
    c: Diameter(g0) = 4
FEATURE [Part::Extrusion] Extrude061
  Base = -> Sketch056
  Dir = (-0.273152,-0.961971,0)
  DirMode = 2
  FaceMakerClass = Part::FaceMakerBullseye
  LengthFwd = 15
  LengthRev = 0
  Solid = true
  Symmetric = true
FEATURE [Sketcher::SketchObject] Sketch057
  FullyConstrained = false
  MapMode = 5
  Placement = pos=(-75.179,-105.322,4) rot=(0.938939,-0.243304,-0.243304;1.63376rad)
  Support = -> [Extrude036]
  sketch-geometry (2):
    g0: Circle CenterX=0 CenterY=20.5924 CenterZ=0 NormalX=0 NormalY=0 NormalZ=1 AngleXU=0 Radius=2
    g1: Circle CenterX=0 CenterY=8.18698 CenterZ=0 NormalX=0 NormalY=0 NormalZ=1 AngleXU=0 Radius=2
  constraints (4):
    c: PointOnObject(g0,g-2)
    c: PointOnObject(g1,g-2)
    c: Diameter(g1) = 4
    c: Diameter(g0) = 4
FEATURE [Part::Extrusion] Extrude062
  Base = -> Sketch057
  Dir = (-0.485643,-0.874157,-3e-16)
  DirMode = 2
  FaceMakerClass = Part::FaceMakerBullseye
  LengthFwd = 15
  LengthRev = 0
  Solid = true
  Symmetric = true
FEATURE [Part::MultiFuse] Fusion021  label="Front 2 Covers Holes"
  Refine = true
  Shapes = -> [Extrude060,Extrude061]
FEATURE [Part::MultiFuse] Fusion022  label="Side Covers Holes"
  Refine = true
  Shapes = -> [Extrude062,Extrude059,Extrude058]
FEATURE [Part::MultiFuse] Fusion023  label="Front 2 Covers Holes001"
  Refine = true
  Shapes = -> [Extrude060,Extrude061]
FEATURE [Part::MultiFuse] Fusion024  label="Front 2 Covers Holes002"
  Refine = true
  Shapes = -> [Extrude060,Extrude061]
FEATURE [Part::Cut] Cut030  label="Front Hit Pannel Layer 1"
  Base = -> Extrude057
  Refine = true
  Tool = -> Fusion021
FEATURE [Part::Cut] Cut031
  Base = -> Extrude036
  Refine = true
  Tool = -> Fusion023
FEATURE [Part::Cut] Cut032
  Base = -> Cut023
  Refine = true
  Tool = -> Fusion024
FEATURE [Part::MultiFuse] Fusion025  label="Side Covers Holes001"
  Refine = true
  Shapes = -> [Extrude062,Extrude059,Extrude058]
FEATURE [Part::Cut] Cut033  label="Front Hit Pannel Layer 2"
  Base = -> Cut031
  Refine = true
  Tool = -> Fusion025
FEATURE [Part::Cut] Cut034  label="Full Holed Body"
  Base = -> Cut032
  Refine = true
  Tool = -> Fusion022
FEATURE [Part::Feature] Part__Feature136  label="PCB MX1508"
  shape: bbox 24.5 x 1.62 x 21.2 mm, 502 faces (baked)
FEATURE [Part::Feature] Part__Feature137  label="smd100uF16VRVT"
  Placement = pos=(3.4012,1.65,-5.66553) rot=(0,-1,0;1.57952rad)
  shape: bbox 8.064 x 5.76 x 9.017 mm, 161 faces, 6 solids (baked)
FEATURE [Part::Feature] Part__Feature138  label="smd100uF16VRVT001"
  Placement = pos=(-3.69416,1.65,-5.66553) rot=(0,1,0;1.55334rad)
  shape: bbox 8.063 x 5.76 x 9.034 mm, 161 faces, 6 solids (baked)
FEATURE [Part::Feature] Part__Feature139  label="smdChip16pin"
  Placement = pos=(0.38974,1.52498,9.68189) rot=(0,1,0;3.14159rad)
  shape: bbox 7.3 x 1.227 x 10 mm, 477 faces, 17 solids (baked)
FEATURE [Part::Feature] Part__Feature140  label="smdResistor2200"
  Placement = pos=(10.7501,0.8,-6.22873) rot=(0,1,0;1.5708rad)
  shape: bbox 1.307 x 0.6262 x 2.511 mm, 79 faces, 3 solids (baked)
FEATURE [Part::Feature] Part__Feature141  label="smdDiode"
  Placement = pos=(8.50324,1.45,-6.59956) rot=(0,1,0;1.5708rad)
  shape: bbox 1.407 x 1.407 x 3.85 mm, 60 faces (baked)
FEATURE [App::Part] MX1508
  Group = -> [Part__Feature136,Part__Feature137,Part__Feature138,Part__Feature139,Part__Feature140,Part__Feature141]
  Origin = -> Origin009
  Placement = pos=(0,7.25,3) rot=(1,0,0;1.5708rad)
FEATURE [Sketcher::SketchObject] Sketch058
  FullyConstrained = true
  MapMode = 5
  Placement = pos=(0,0,37) rot=(0,0,1;0rad)
  Support = -> [Cut022]
  sketch-geometry (4):
    g0: LineSegment StartX=-31 StartY=-35 StartZ=0 EndX=-18 EndY=-35 EndZ=0
    g1: LineSegment StartX=-18 StartY=-35 StartZ=0 EndX=-18 EndY=-75 EndZ=0
    g2: LineSegment StartX=-18 StartY=-75 StartZ=0 EndX=-31 EndY=-75 EndZ=0
    g3: LineSegment StartX=-31 StartY=-75 StartZ=0 EndX=-31 EndY=-35 EndZ=0
  constraints (12):
    c: Coincident(g0,g1)
    c: Coincident(g1,g2)
    c: Coincident(g2,g3)
    c: Coincident(g3,g0)
    c: Horizontal(g0)
    c: Horizontal(g2)
    c: Vertical(g1)
    c: Vertical(g3)
    c: DistanceX(g0,g-1) = 18
    c: DistanceY(g0,g-1) = 35
    c: DistanceY(g1,g1) = 40
    c: DistanceX(g0,g0) = 13
FEATURE [Part::Extrusion] Extrude063  label="Axe Hit Gap"
  Base = -> Sketch058
  Dir = (0,0,1)
  DirMode = 2
  FaceMakerClass = Part::FaceMakerBullseye
  LengthFwd = 15
  LengthRev = 0
  Solid = true
  Symmetric = true
FEATURE [Part::Cut] Cut035  label="Lid"
  Base = -> Cut022
  Refine = true
  Tool = -> Extrude063
FEATURE [Sketcher::SketchObject] Sketch059
  FullyConstrained = true
  Placement = pos=(0,0,0) rot=(0.57735,0.57735,0.57735;2.0944rad)
  sketch-geometry (12):
    g0: LineSegment StartX=-65.71 StartY=39.18 StartZ=0 EndX=-65.71 EndY=37.18 EndZ=0
    g1: LineSegment StartX=-65.71 StartY=37.18 StartZ=0 EndX=-57.71 EndY=37.18 EndZ=0
    g2: LineSegment StartX=-57.71 StartY=37.18 StartZ=0 EndX=-57.71 EndY=45.18 EndZ=0
    g3: LineSegment StartX=-57.71 StartY=45.18 StartZ=0 EndX=-44.81 EndY=45.18 EndZ=0
    g4: LineSegment StartX=-44.81 StartY=45.18 StartZ=0 EndX=-44.81 EndY=37.18 EndZ=0
    g5: LineSegment StartX=-44.81 StartY=37.18 StartZ=0 EndX=-36.81 EndY=37.18 EndZ=0
    g6: LineSegment StartX=-36.81 StartY=37.18 StartZ=0 EndX=-36.81 EndY=39.18 EndZ=0
    g7: LineSegment StartX=-36.81 StartY=39.18 StartZ=0 EndX=-42.81 EndY=39.18 EndZ=0
    g8: LineSegment StartX=-42.81 StartY=39.18 StartZ=0 EndX=-42.81 EndY=47.18 EndZ=0
    g9: LineSegment StartX=-42.81 StartY=47.18 StartZ=0 EndX=-59.71 EndY=47.18 EndZ=0
    g10: LineSegment StartX=-59.71 StartY=47.18 StartZ=0 EndX=-59.71 EndY=39.18 EndZ=0
    g11: LineSegment StartX=-59.71 StartY=39.18 StartZ=0 EndX=-65.71 EndY=39.18 EndZ=0
  constraints (36):
    c: Vertical(g0)
    c: Coincident(g0,g1)
    c: Horizontal(g1)
    c: Coincident(g1,g2)
    c: Vertical(g2)
    c: Coincident(g2,g3)
    c: Horizontal(g3)
    c: Coincident(g3,g4)
    c: Vertical(g4)
    c: Coincident(g4,g5)
    c: Horizontal(g5)
    c: Coincident(g5,g6)
    c: Vertical(g6)
    c: Coincident(g6,g7)
    c: Horizontal(g7)
    c: Coincident(g7,g8)
    c: Vertical(g8)
    c: Coincident(g8,g9)
    c: Horizontal(g9)
    c: Coincident(g9,g10)
    c: Vertical(g10)
    c: Coincident(g10,g11)
    c: Coincident(g11,g0)
    c: Horizontal(g11)
    c: DistanceY(g0,g0) = 2
    c: Distance(g0,g-1) = 37.18
    c: DistanceX(g11,g11) = 6
    c: DistanceX(g-2,g0) = -65.71
    c: DistanceY(g10,g10) = 8
    c: Distance(g2,g9) = 2
    c: Distance(g2,g10) = 2
    c: DistanceX(g9,g9) = 16.9
    c: Distance(g3,g8) = 2
    c: DistanceY(g6,g6) = 2
    c: DistanceY(g8,g8) = 8
    c: DistanceX(g7,g7) = 6
FEATURE [Part::Extrusion] Extrude064  label="Servo Holder"
  Base = -> Sketch059
  Dir = (1,0,0)
  DirMode = 2
  FaceMakerClass = Part::FaceMakerBullseye
  LengthFwd = 15
  LengthRev = 0
  Solid = true
  Symmetric = true
FEATURE [Sketcher::SketchObject] Sketch060
  FullyConstrained = false
  MapMode = 5
  Placement = pos=(0,0,39.18) rot=(0,0,1;0rad)
  Support = -> [Extrude064]
  sketch-geometry (2):
    g0: Circle CenterX=0 CenterY=-40.2077 CenterZ=0 NormalX=0 NormalY=0 NormalZ=1 AngleXU=0 Radius=1.5
    g1: Circle CenterX=0 CenterY=-62.2828 CenterZ=0 NormalX=0 NormalY=0 NormalZ=1 AngleXU=0 Radius=1.5
  constraints (4):
    c: PointOnObject(g0,g-2)
    c: Diameter(g0) = 3
    c: PointOnObject(g1,g-2)
    c: Diameter(g1) = 3
FEATURE [Part::Extrusion] Extrude065  label="Screw Gaps"
  Base = -> Sketch060
  Dir = (0,0,1)
  DirMode = 2
  FaceMakerClass = Part::FaceMakerBullseye
  LengthFwd = 10
  LengthRev = 0
  Solid = true
  Symmetric = true
FEATURE [Part::Cut] Cut036  label="Servo Fixer"
  Base = -> Extrude064
  Placement = pos=(2.5,0,0) rot=(0,0,1;0rad)
  Refine = true
  Tool = -> Extrude065
note: 1 file-system path scrubbed to <path> (originals preserved in the JSON sidecar)
